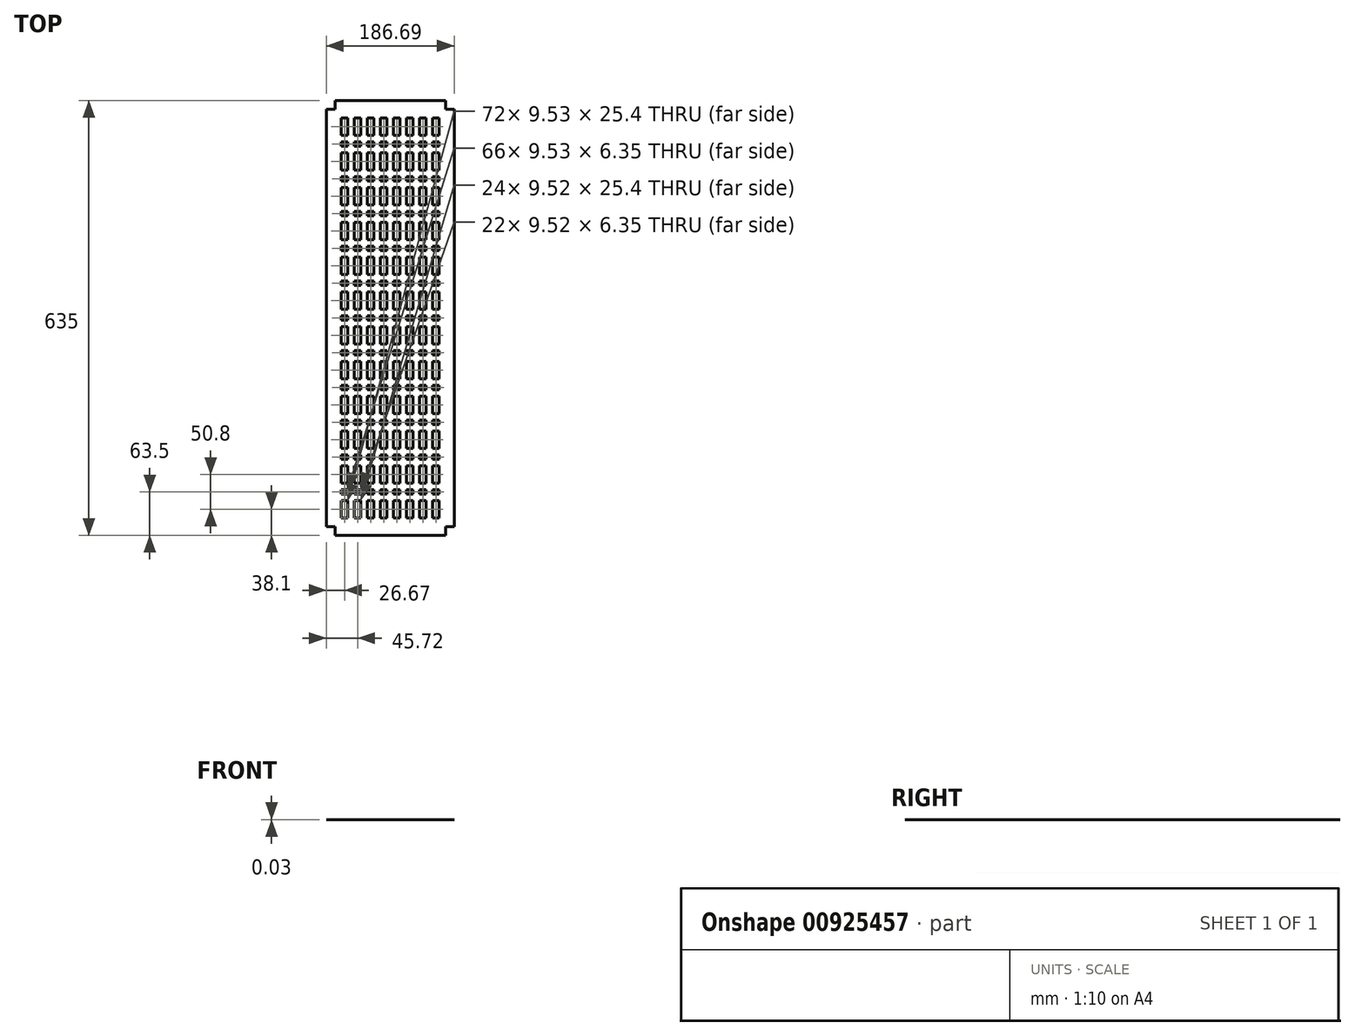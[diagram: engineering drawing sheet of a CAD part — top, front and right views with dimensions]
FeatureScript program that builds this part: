
annotation { "Feature Type Name" : "Feature", "Feature Type Description" : "" }
export const myFeature = defineFeature(function(context is Context, id is Id, definition is map)
    precondition{}
    {
        {
            var Q0;
            Q0=qCreatedBy(makeId("Top.planeOp"),FACE);
            var sketch = newSketch(context, id + "F0", { "sketchPlane" : qUnion([Q0])});
            skLineSegment(sketch, "E0", {"start": v(0, 0) * mm, "end": v(0, 12.7) * mm});
            skLineSegment(sketch, "E1", {"start": v(0, 12.7) * mm, "end": v(161.3, 12.7) * mm});
            skLineSegment(sketch, "E2", {"start": v(161.3, 12.7) * mm, "end": v(161.3, 0) * mm});
            skLineSegment(sketch, "E3", {"start": v(161.3, 0) * mm, "end": v(174, 0) * mm});
            skLineSegment(sketch, "E4", {"start": v(174, 0) * mm, "end": v(174, -609.6) * mm});
            skLineSegment(sketch, "E5", {"start": v(174, -609.6) * mm, "end": v(161.3, -609.6) * mm});
            skLineSegment(sketch, "E6", {"start": v(161.3, -609.6) * mm, "end": v(161.3, -622.3) * mm});
            skLineSegment(sketch, "E7", {"start": v(161.3, -622.3) * mm, "end": v(0, -622.3) * mm});
            skLineSegment(sketch, "E8", {"start": v(0, -622.3) * mm, "end": v(0, -609.6) * mm});
            skLineSegment(sketch, "E9", {"start": v(0, -609.6) * mm, "end": v(-12.7, -609.6) * mm});
            skLineSegment(sketch, "E10", {"start": v(-12.7, -609.6) * mm, "end": v(-12.7, 0) * mm});
            skLineSegment(sketch, "E11", {"start": v(-12.7, 0) * mm, "end": v(0, 0) * mm});
            skSolve(sketch);
        }
        {
            var Q0;
            Q0 = qSketchRegion(id + "F0", true);
            extrude(context, id + "F1", {"entities" : qUnion([Q0]), "depth" : 0.03 * mm, "offsetDistance" : 25.4 * mm});
        }
        {
            var Q0;
            Q0=makeQuery(id+"F1.opExtrude","CAP_FACE",FACE,{"disambiguationData":[OSD([sQuery(id+"F0.wireOp",EDGE,"E0"),sQuery(id+"F0.wireOp",EDGE,"E1"),sQuery(id+"F0.wireOp",EDGE,"E2"),sQuery(id+"F0.wireOp",EDGE,"E3"),sQuery(id+"F0.wireOp",EDGE,"E4"),sQuery(id+"F0.wireOp",EDGE,"E5"),sQuery(id+"F0.wireOp",EDGE,"E6"),sQuery(id+"F0.wireOp",EDGE,"E7"),sQuery(id+"F0.wireOp",EDGE,"E8"),sQuery(id+"F0.wireOp",EDGE,"E9"),sQuery(id+"F0.wireOp",EDGE,"E10"),sQuery(id+"F0.wireOp",EDGE,"E11")])],"isStart":false});
            var sketch = newSketch(context, id + "F2", { "sketchPlane" : qUnion([Q0])});
            skLineSegment(sketch, "E12", {"start": v(80.65, 12.7) * mm, "end": v(80.65, -622.3) * mm, "construction": true});
            skLineSegment(sketch, "E13.bottom", {"start": v(75.88, -12.7) * mm, "end": v(66.36, -12.7) * mm});
            skLineSegment(sketch, "E13.top", {"start": v(75.88, -38.1) * mm, "end": v(66.36, -38.1) * mm});
            skLineSegment(sketch, "E13.left", {"start": v(75.88, -12.7) * mm, "end": v(75.88, -38.1) * mm});
            skLineSegment(sketch, "E13.right", {"start": v(66.36, -12.7) * mm, "end": v(66.36, -38.1) * mm});
            skLineSegment(sketch, "E14.bottom", {"start": v(66.36, -47.63) * mm, "end": v(75.88, -47.63) * mm});
            skLineSegment(sketch, "E14.top", {"start": v(66.36, -53.98) * mm, "end": v(75.88, -53.98) * mm});
            skLineSegment(sketch, "E14.left", {"start": v(66.36, -47.63) * mm, "end": v(66.36, -53.98) * mm});
            skLineSegment(sketch, "E14.right", {"start": v(75.88, -47.63) * mm, "end": v(75.88, -53.98) * mm});
            skLineSegment(sketch, "E15.0.1.0", {"start": v(66.36, -63.5) * mm, "end": v(66.36, -88.9) * mm});
            skLineSegment(sketch, "E15.0.1.1", {"start": v(75.88, -63.5) * mm, "end": v(66.36, -63.5) * mm});
            skLineSegment(sketch, "E15.0.1.2", {"start": v(75.88, -63.5) * mm, "end": v(75.88, -88.9) * mm});
            skLineSegment(sketch, "E15.0.1.3", {"start": v(75.88, -88.9) * mm, "end": v(66.36, -88.9) * mm});
            skLineSegment(sketch, "E15.0.1.4", {"start": v(66.36, -98.43) * mm, "end": v(75.88, -98.43) * mm});
            skLineSegment(sketch, "E15.0.1.5", {"start": v(75.88, -98.43) * mm, "end": v(75.88, -104.78) * mm});
            skLineSegment(sketch, "E15.0.1.6", {"start": v(66.36, -104.78) * mm, "end": v(75.88, -104.78) * mm});
            skLineSegment(sketch, "E15.0.1.7", {"start": v(66.36, -98.43) * mm, "end": v(66.36, -104.78) * mm});
            skLineSegment(sketch, "E15.0.2.0", {"start": v(66.36, -114.3) * mm, "end": v(66.36, -139.7) * mm});
            skLineSegment(sketch, "E15.0.2.1", {"start": v(75.88, -114.3) * mm, "end": v(66.36, -114.3) * mm});
            skLineSegment(sketch, "E15.0.2.2", {"start": v(75.88, -114.3) * mm, "end": v(75.88, -139.7) * mm});
            skLineSegment(sketch, "E15.0.2.3", {"start": v(75.88, -139.7) * mm, "end": v(66.36, -139.7) * mm});
            skLineSegment(sketch, "E15.0.2.4", {"start": v(66.36, -149.22) * mm, "end": v(75.88, -149.22) * mm});
            skLineSegment(sketch, "E15.0.2.5", {"start": v(75.88, -149.23) * mm, "end": v(75.88, -155.58) * mm});
            skLineSegment(sketch, "E15.0.2.6", {"start": v(66.36, -155.58) * mm, "end": v(75.88, -155.58) * mm});
            skLineSegment(sketch, "E15.0.2.7", {"start": v(66.36, -149.23) * mm, "end": v(66.36, -155.58) * mm});
            skLineSegment(sketch, "E15.0.3.0", {"start": v(66.36, -165.1) * mm, "end": v(66.36, -190.5) * mm});
            skLineSegment(sketch, "E15.0.3.1", {"start": v(75.88, -165.1) * mm, "end": v(66.36, -165.1) * mm});
            skLineSegment(sketch, "E15.0.3.2", {"start": v(75.88, -165.1) * mm, "end": v(75.88, -190.5) * mm});
            skLineSegment(sketch, "E15.0.3.3", {"start": v(75.88, -190.5) * mm, "end": v(66.36, -190.5) * mm});
            skLineSegment(sketch, "E15.0.3.4", {"start": v(66.36, -200.02) * mm, "end": v(75.88, -200.02) * mm});
            skLineSegment(sketch, "E15.0.3.5", {"start": v(75.88, -200.02) * mm, "end": v(75.88, -206.37) * mm});
            skLineSegment(sketch, "E15.0.3.6", {"start": v(66.36, -206.37) * mm, "end": v(75.88, -206.37) * mm});
            skLineSegment(sketch, "E15.0.3.7", {"start": v(66.36, -200.02) * mm, "end": v(66.36, -206.37) * mm});
            skLineSegment(sketch, "E15.0.4.0", {"start": v(66.36, -215.9) * mm, "end": v(66.36, -241.3) * mm});
            skLineSegment(sketch, "E15.0.4.1", {"start": v(75.88, -215.9) * mm, "end": v(66.36, -215.9) * mm});
            skLineSegment(sketch, "E15.0.4.2", {"start": v(75.88, -215.9) * mm, "end": v(75.88, -241.3) * mm});
            skLineSegment(sketch, "E15.0.4.3", {"start": v(75.88, -241.3) * mm, "end": v(66.36, -241.3) * mm});
            skLineSegment(sketch, "E15.0.4.4", {"start": v(66.36, -250.83) * mm, "end": v(75.88, -250.83) * mm});
            skLineSegment(sketch, "E15.0.4.5", {"start": v(75.88, -250.82) * mm, "end": v(75.88, -257.18) * mm});
            skLineSegment(sketch, "E15.0.4.6", {"start": v(66.36, -257.18) * mm, "end": v(75.88, -257.18) * mm});
            skLineSegment(sketch, "E15.0.4.7", {"start": v(66.36, -250.82) * mm, "end": v(66.36, -257.18) * mm});
            skLineSegment(sketch, "E15.0.5.0", {"start": v(66.36, -266.7) * mm, "end": v(66.36, -292.1) * mm});
            skLineSegment(sketch, "E15.0.5.1", {"start": v(75.88, -266.7) * mm, "end": v(66.36, -266.7) * mm});
            skLineSegment(sketch, "E15.0.5.2", {"start": v(75.88, -266.7) * mm, "end": v(75.88, -292.1) * mm});
            skLineSegment(sketch, "E15.0.5.3", {"start": v(75.88, -292.1) * mm, "end": v(66.36, -292.1) * mm});
            skLineSegment(sketch, "E15.0.5.4", {"start": v(66.36, -301.63) * mm, "end": v(75.88, -301.63) * mm});
            skLineSegment(sketch, "E15.0.5.5", {"start": v(75.88, -301.62) * mm, "end": v(75.88, -307.98) * mm});
            skLineSegment(sketch, "E15.0.5.6", {"start": v(66.36, -307.98) * mm, "end": v(75.88, -307.98) * mm});
            skLineSegment(sketch, "E15.0.5.7", {"start": v(66.36, -301.62) * mm, "end": v(66.36, -307.98) * mm});
            skLineSegment(sketch, "E15.0.6.0", {"start": v(66.36, -317.5) * mm, "end": v(66.36, -342.9) * mm});
            skLineSegment(sketch, "E15.0.6.1", {"start": v(75.88, -317.5) * mm, "end": v(66.36, -317.5) * mm});
            skLineSegment(sketch, "E15.0.6.2", {"start": v(75.88, -317.5) * mm, "end": v(75.88, -342.9) * mm});
            skLineSegment(sketch, "E15.0.6.3", {"start": v(75.88, -342.9) * mm, "end": v(66.36, -342.9) * mm});
            skLineSegment(sketch, "E15.0.6.4", {"start": v(66.36, -352.43) * mm, "end": v(75.88, -352.43) * mm});
            skLineSegment(sketch, "E15.0.6.5", {"start": v(75.88, -352.42) * mm, "end": v(75.88, -358.77) * mm});
            skLineSegment(sketch, "E15.0.6.6", {"start": v(66.36, -358.77) * mm, "end": v(75.88, -358.77) * mm});
            skLineSegment(sketch, "E15.0.6.7", {"start": v(66.36, -352.42) * mm, "end": v(66.36, -358.77) * mm});
            skLineSegment(sketch, "E15.0.7.0", {"start": v(66.36, -368.3) * mm, "end": v(66.36, -393.7) * mm});
            skLineSegment(sketch, "E15.0.7.1", {"start": v(75.88, -368.3) * mm, "end": v(66.36, -368.3) * mm});
            skLineSegment(sketch, "E15.0.7.2", {"start": v(75.88, -368.3) * mm, "end": v(75.88, -393.7) * mm});
            skLineSegment(sketch, "E15.0.7.3", {"start": v(75.88, -393.7) * mm, "end": v(66.36, -393.7) * mm});
            skLineSegment(sketch, "E15.0.7.4", {"start": v(66.36, -403.23) * mm, "end": v(75.88, -403.23) * mm});
            skLineSegment(sketch, "E15.0.7.5", {"start": v(75.88, -403.22) * mm, "end": v(75.88, -409.57) * mm});
            skLineSegment(sketch, "E15.0.7.6", {"start": v(66.36, -409.57) * mm, "end": v(75.88, -409.57) * mm});
            skLineSegment(sketch, "E15.0.7.7", {"start": v(66.36, -403.22) * mm, "end": v(66.36, -409.57) * mm});
            skLineSegment(sketch, "E15.0.8.0", {"start": v(66.36, -419.1) * mm, "end": v(66.36, -444.5) * mm});
            skLineSegment(sketch, "E15.0.8.1", {"start": v(75.88, -419.1) * mm, "end": v(66.36, -419.1) * mm});
            skLineSegment(sketch, "E15.0.8.2", {"start": v(75.88, -419.1) * mm, "end": v(75.88, -444.5) * mm});
            skLineSegment(sketch, "E15.0.8.3", {"start": v(75.88, -444.5) * mm, "end": v(66.36, -444.5) * mm});
            skLineSegment(sketch, "E15.0.8.4", {"start": v(66.36, -454.03) * mm, "end": v(75.88, -454.03) * mm});
            skLineSegment(sketch, "E15.0.8.5", {"start": v(75.88, -454.02) * mm, "end": v(75.88, -460.38) * mm});
            skLineSegment(sketch, "E15.0.8.6", {"start": v(66.36, -460.38) * mm, "end": v(75.88, -460.38) * mm});
            skLineSegment(sketch, "E15.0.8.7", {"start": v(66.36, -454.02) * mm, "end": v(66.36, -460.38) * mm});
            skLineSegment(sketch, "E15.0.9.0", {"start": v(66.36, -469.9) * mm, "end": v(66.36, -495.3) * mm});
            skLineSegment(sketch, "E15.0.9.1", {"start": v(75.88, -469.9) * mm, "end": v(66.36, -469.9) * mm});
            skLineSegment(sketch, "E15.0.9.2", {"start": v(75.88, -469.9) * mm, "end": v(75.88, -495.3) * mm});
            skLineSegment(sketch, "E15.0.9.3", {"start": v(75.88, -495.3) * mm, "end": v(66.36, -495.3) * mm});
            skLineSegment(sketch, "E15.0.9.4", {"start": v(66.36, -504.82) * mm, "end": v(75.88, -504.82) * mm});
            skLineSegment(sketch, "E15.0.9.5", {"start": v(75.88, -504.82) * mm, "end": v(75.88, -511.17) * mm});
            skLineSegment(sketch, "E15.0.9.6", {"start": v(66.36, -511.18) * mm, "end": v(75.88, -511.18) * mm});
            skLineSegment(sketch, "E15.0.9.7", {"start": v(66.36, -504.82) * mm, "end": v(66.36, -511.17) * mm});
            skLineSegment(sketch, "E15.0.10.0", {"start": v(66.36, -520.7) * mm, "end": v(66.36, -546.1) * mm});
            skLineSegment(sketch, "E15.0.10.1", {"start": v(75.88, -520.7) * mm, "end": v(66.36, -520.7) * mm});
            skLineSegment(sketch, "E15.0.10.2", {"start": v(75.88, -520.7) * mm, "end": v(75.88, -546.1) * mm});
            skLineSegment(sketch, "E15.0.10.3", {"start": v(75.88, -546.1) * mm, "end": v(66.36, -546.1) * mm});
            skLineSegment(sketch, "E15.0.10.4", {"start": v(66.36, -555.62) * mm, "end": v(75.88, -555.62) * mm});
            skLineSegment(sketch, "E15.0.10.5", {"start": v(75.88, -555.62) * mm, "end": v(75.88, -561.98) * mm});
            skLineSegment(sketch, "E15.0.10.6", {"start": v(66.36, -561.98) * mm, "end": v(75.88, -561.98) * mm});
            skLineSegment(sketch, "E15.0.10.7", {"start": v(66.36, -555.62) * mm, "end": v(66.36, -561.98) * mm});
            skLineSegment(sketch, "E15.0.11.0", {"start": v(66.36, -571.5) * mm, "end": v(66.36, -596.9) * mm});
            skLineSegment(sketch, "E15.0.11.1", {"start": v(75.88, -571.5) * mm, "end": v(66.36, -571.5) * mm});
            skLineSegment(sketch, "E15.0.11.2", {"start": v(75.88, -571.5) * mm, "end": v(75.88, -596.9) * mm});
            skLineSegment(sketch, "E15.0.11.3", {"start": v(75.88, -596.9) * mm, "end": v(66.36, -596.9) * mm});
            skLineSegment(sketch, "E15.1.0.0", {"start": v(47.3, -12.7) * mm, "end": v(47.3, -38.1) * mm});
            skLineSegment(sketch, "E15.1.0.1", {"start": v(56.83, -12.7) * mm, "end": v(47.3, -12.7) * mm});
            skLineSegment(sketch, "E15.1.0.2", {"start": v(56.83, -12.7) * mm, "end": v(56.83, -38.1) * mm});
            skLineSegment(sketch, "E15.1.0.3", {"start": v(56.83, -38.1) * mm, "end": v(47.3, -38.1) * mm});
            skLineSegment(sketch, "E15.1.0.4", {"start": v(47.3, -47.63) * mm, "end": v(56.83, -47.63) * mm});
            skLineSegment(sketch, "E15.1.0.5", {"start": v(56.83, -47.63) * mm, "end": v(56.83, -53.98) * mm});
            skLineSegment(sketch, "E15.1.0.6", {"start": v(47.3, -53.98) * mm, "end": v(56.83, -53.98) * mm});
            skLineSegment(sketch, "E15.1.0.7", {"start": v(47.3, -47.63) * mm, "end": v(47.3, -53.98) * mm});
            skLineSegment(sketch, "E15.1.1.0", {"start": v(47.3, -63.5) * mm, "end": v(47.3, -88.9) * mm});
            skLineSegment(sketch, "E15.1.1.1", {"start": v(56.83, -63.5) * mm, "end": v(47.3, -63.5) * mm});
            skLineSegment(sketch, "E15.1.1.2", {"start": v(56.83, -63.5) * mm, "end": v(56.83, -88.9) * mm});
            skLineSegment(sketch, "E15.1.1.3", {"start": v(56.83, -88.9) * mm, "end": v(47.3, -88.9) * mm});
            skLineSegment(sketch, "E15.1.1.4", {"start": v(47.3, -98.43) * mm, "end": v(56.83, -98.43) * mm});
            skLineSegment(sketch, "E15.1.1.5", {"start": v(56.83, -98.43) * mm, "end": v(56.83, -104.78) * mm});
            skLineSegment(sketch, "E15.1.1.6", {"start": v(47.3, -104.78) * mm, "end": v(56.83, -104.78) * mm});
            skLineSegment(sketch, "E15.1.1.7", {"start": v(47.3, -98.43) * mm, "end": v(47.3, -104.78) * mm});
            skLineSegment(sketch, "E15.1.2.0", {"start": v(47.3, -114.3) * mm, "end": v(47.3, -139.7) * mm});
            skLineSegment(sketch, "E15.1.2.1", {"start": v(56.83, -114.3) * mm, "end": v(47.3, -114.3) * mm});
            skLineSegment(sketch, "E15.1.2.2", {"start": v(56.83, -114.3) * mm, "end": v(56.83, -139.7) * mm});
            skLineSegment(sketch, "E15.1.2.3", {"start": v(56.83, -139.7) * mm, "end": v(47.3, -139.7) * mm});
            skLineSegment(sketch, "E15.1.2.4", {"start": v(47.3, -149.22) * mm, "end": v(56.83, -149.22) * mm});
            skLineSegment(sketch, "E15.1.2.5", {"start": v(56.83, -149.23) * mm, "end": v(56.83, -155.58) * mm});
            skLineSegment(sketch, "E15.1.2.6", {"start": v(47.3, -155.58) * mm, "end": v(56.83, -155.58) * mm});
            skLineSegment(sketch, "E15.1.2.7", {"start": v(47.3, -149.23) * mm, "end": v(47.3, -155.58) * mm});
            skLineSegment(sketch, "E15.1.3.0", {"start": v(47.3, -165.1) * mm, "end": v(47.3, -190.5) * mm});
            skLineSegment(sketch, "E15.1.3.1", {"start": v(56.83, -165.1) * mm, "end": v(47.3, -165.1) * mm});
            skLineSegment(sketch, "E15.1.3.2", {"start": v(56.83, -165.1) * mm, "end": v(56.83, -190.5) * mm});
            skLineSegment(sketch, "E15.1.3.3", {"start": v(56.83, -190.5) * mm, "end": v(47.3, -190.5) * mm});
            skLineSegment(sketch, "E15.1.3.4", {"start": v(47.3, -200.02) * mm, "end": v(56.83, -200.02) * mm});
            skLineSegment(sketch, "E15.1.3.5", {"start": v(56.83, -200.02) * mm, "end": v(56.83, -206.37) * mm});
            skLineSegment(sketch, "E15.1.3.6", {"start": v(47.3, -206.37) * mm, "end": v(56.83, -206.37) * mm});
            skLineSegment(sketch, "E15.1.3.7", {"start": v(47.3, -200.02) * mm, "end": v(47.3, -206.37) * mm});
            skLineSegment(sketch, "E15.1.4.0", {"start": v(47.3, -215.9) * mm, "end": v(47.3, -241.3) * mm});
            skLineSegment(sketch, "E15.1.4.1", {"start": v(56.83, -215.9) * mm, "end": v(47.3, -215.9) * mm});
            skLineSegment(sketch, "E15.1.4.2", {"start": v(56.83, -215.9) * mm, "end": v(56.83, -241.3) * mm});
            skLineSegment(sketch, "E15.1.4.3", {"start": v(56.83, -241.3) * mm, "end": v(47.3, -241.3) * mm});
            skLineSegment(sketch, "E15.1.4.4", {"start": v(47.3, -250.83) * mm, "end": v(56.83, -250.83) * mm});
            skLineSegment(sketch, "E15.1.4.5", {"start": v(56.83, -250.82) * mm, "end": v(56.83, -257.18) * mm});
            skLineSegment(sketch, "E15.1.4.6", {"start": v(47.3, -257.18) * mm, "end": v(56.83, -257.18) * mm});
            skLineSegment(sketch, "E15.1.4.7", {"start": v(47.3, -250.82) * mm, "end": v(47.3, -257.18) * mm});
            skLineSegment(sketch, "E15.1.5.0", {"start": v(47.3, -266.7) * mm, "end": v(47.3, -292.1) * mm});
            skLineSegment(sketch, "E15.1.5.1", {"start": v(56.83, -266.7) * mm, "end": v(47.3, -266.7) * mm});
            skLineSegment(sketch, "E15.1.5.2", {"start": v(56.83, -266.7) * mm, "end": v(56.83, -292.1) * mm});
            skLineSegment(sketch, "E15.1.5.3", {"start": v(56.83, -292.1) * mm, "end": v(47.3, -292.1) * mm});
            skLineSegment(sketch, "E15.1.5.4", {"start": v(47.3, -301.63) * mm, "end": v(56.83, -301.63) * mm});
            skLineSegment(sketch, "E15.1.5.5", {"start": v(56.83, -301.62) * mm, "end": v(56.83, -307.98) * mm});
            skLineSegment(sketch, "E15.1.5.6", {"start": v(47.3, -307.98) * mm, "end": v(56.83, -307.98) * mm});
            skLineSegment(sketch, "E15.1.5.7", {"start": v(47.3, -301.62) * mm, "end": v(47.3, -307.98) * mm});
            skLineSegment(sketch, "E15.1.6.0", {"start": v(47.3, -317.5) * mm, "end": v(47.3, -342.9) * mm});
            skLineSegment(sketch, "E15.1.6.1", {"start": v(56.83, -317.5) * mm, "end": v(47.3, -317.5) * mm});
            skLineSegment(sketch, "E15.1.6.2", {"start": v(56.83, -317.5) * mm, "end": v(56.83, -342.9) * mm});
            skLineSegment(sketch, "E15.1.6.3", {"start": v(56.83, -342.9) * mm, "end": v(47.3, -342.9) * mm});
            skLineSegment(sketch, "E15.1.6.4", {"start": v(47.3, -352.43) * mm, "end": v(56.83, -352.43) * mm});
            skLineSegment(sketch, "E15.1.6.5", {"start": v(56.83, -352.42) * mm, "end": v(56.83, -358.77) * mm});
            skLineSegment(sketch, "E15.1.6.6", {"start": v(47.3, -358.77) * mm, "end": v(56.83, -358.77) * mm});
            skLineSegment(sketch, "E15.1.6.7", {"start": v(47.3, -352.42) * mm, "end": v(47.3, -358.77) * mm});
            skLineSegment(sketch, "E15.1.7.0", {"start": v(47.3, -368.3) * mm, "end": v(47.3, -393.7) * mm});
            skLineSegment(sketch, "E15.1.7.1", {"start": v(56.83, -368.3) * mm, "end": v(47.3, -368.3) * mm});
            skLineSegment(sketch, "E15.1.7.2", {"start": v(56.83, -368.3) * mm, "end": v(56.83, -393.7) * mm});
            skLineSegment(sketch, "E15.1.7.3", {"start": v(56.83, -393.7) * mm, "end": v(47.3, -393.7) * mm});
            skLineSegment(sketch, "E15.1.7.4", {"start": v(47.3, -403.23) * mm, "end": v(56.83, -403.23) * mm});
            skLineSegment(sketch, "E15.1.7.5", {"start": v(56.83, -403.22) * mm, "end": v(56.83, -409.57) * mm});
            skLineSegment(sketch, "E15.1.7.6", {"start": v(47.3, -409.57) * mm, "end": v(56.83, -409.57) * mm});
            skLineSegment(sketch, "E15.1.7.7", {"start": v(47.3, -403.22) * mm, "end": v(47.3, -409.57) * mm});
            skLineSegment(sketch, "E15.1.8.0", {"start": v(47.3, -419.1) * mm, "end": v(47.3, -444.5) * mm});
            skLineSegment(sketch, "E15.1.8.1", {"start": v(56.83, -419.1) * mm, "end": v(47.3, -419.1) * mm});
            skLineSegment(sketch, "E15.1.8.2", {"start": v(56.83, -419.1) * mm, "end": v(56.83, -444.5) * mm});
            skLineSegment(sketch, "E15.1.8.3", {"start": v(56.83, -444.5) * mm, "end": v(47.3, -444.5) * mm});
            skLineSegment(sketch, "E15.1.8.4", {"start": v(47.3, -454.03) * mm, "end": v(56.83, -454.03) * mm});
            skLineSegment(sketch, "E15.1.8.5", {"start": v(56.83, -454.02) * mm, "end": v(56.83, -460.38) * mm});
            skLineSegment(sketch, "E15.1.8.6", {"start": v(47.3, -460.38) * mm, "end": v(56.83, -460.38) * mm});
            skLineSegment(sketch, "E15.1.8.7", {"start": v(47.3, -454.02) * mm, "end": v(47.3, -460.38) * mm});
            skLineSegment(sketch, "E15.1.9.0", {"start": v(47.3, -469.9) * mm, "end": v(47.3, -495.3) * mm});
            skLineSegment(sketch, "E15.1.9.1", {"start": v(56.83, -469.9) * mm, "end": v(47.3, -469.9) * mm});
            skLineSegment(sketch, "E15.1.9.2", {"start": v(56.83, -469.9) * mm, "end": v(56.83, -495.3) * mm});
            skLineSegment(sketch, "E15.1.9.3", {"start": v(56.83, -495.3) * mm, "end": v(47.3, -495.3) * mm});
            skLineSegment(sketch, "E15.1.9.4", {"start": v(47.3, -504.82) * mm, "end": v(56.83, -504.82) * mm});
            skLineSegment(sketch, "E15.1.9.5", {"start": v(56.83, -504.82) * mm, "end": v(56.83, -511.17) * mm});
            skLineSegment(sketch, "E15.1.9.6", {"start": v(47.3, -511.18) * mm, "end": v(56.83, -511.18) * mm});
            skLineSegment(sketch, "E15.1.9.7", {"start": v(47.3, -504.82) * mm, "end": v(47.3, -511.17) * mm});
            skLineSegment(sketch, "E15.1.10.0", {"start": v(47.3, -520.7) * mm, "end": v(47.3, -546.1) * mm});
            skLineSegment(sketch, "E15.1.10.1", {"start": v(56.83, -520.7) * mm, "end": v(47.3, -520.7) * mm});
            skLineSegment(sketch, "E15.1.10.2", {"start": v(56.83, -520.7) * mm, "end": v(56.83, -546.1) * mm});
            skLineSegment(sketch, "E15.1.10.3", {"start": v(56.83, -546.1) * mm, "end": v(47.3, -546.1) * mm});
            skLineSegment(sketch, "E15.1.10.4", {"start": v(47.3, -555.62) * mm, "end": v(56.83, -555.62) * mm});
            skLineSegment(sketch, "E15.1.10.5", {"start": v(56.83, -555.62) * mm, "end": v(56.83, -561.98) * mm});
            skLineSegment(sketch, "E15.1.10.6", {"start": v(47.3, -561.98) * mm, "end": v(56.83, -561.98) * mm});
            skLineSegment(sketch, "E15.1.10.7", {"start": v(47.3, -555.62) * mm, "end": v(47.3, -561.98) * mm});
            skLineSegment(sketch, "E15.1.11.0", {"start": v(47.3, -571.5) * mm, "end": v(47.3, -596.9) * mm});
            skLineSegment(sketch, "E15.1.11.1", {"start": v(56.83, -571.5) * mm, "end": v(47.3, -571.5) * mm});
            skLineSegment(sketch, "E15.1.11.2", {"start": v(56.83, -571.5) * mm, "end": v(56.83, -596.9) * mm});
            skLineSegment(sketch, "E15.1.11.3", {"start": v(56.83, -596.9) * mm, "end": v(47.3, -596.9) * mm});
            skLineSegment(sketch, "E15.2.0.0", {"start": v(28.26, -12.7) * mm, "end": v(28.26, -38.1) * mm});
            skLineSegment(sketch, "E15.2.0.1", {"start": v(37.78, -12.7) * mm, "end": v(28.26, -12.7) * mm});
            skLineSegment(sketch, "E15.2.0.2", {"start": v(37.78, -12.7) * mm, "end": v(37.78, -38.1) * mm});
            skLineSegment(sketch, "E15.2.0.3", {"start": v(37.78, -38.1) * mm, "end": v(28.26, -38.1) * mm});
            skLineSegment(sketch, "E15.2.0.4", {"start": v(28.26, -47.63) * mm, "end": v(37.78, -47.63) * mm});
            skLineSegment(sketch, "E15.2.0.5", {"start": v(37.78, -47.63) * mm, "end": v(37.78, -53.98) * mm});
            skLineSegment(sketch, "E15.2.0.6", {"start": v(28.26, -53.98) * mm, "end": v(37.78, -53.98) * mm});
            skLineSegment(sketch, "E15.2.0.7", {"start": v(28.26, -47.63) * mm, "end": v(28.26, -53.98) * mm});
            skLineSegment(sketch, "E15.2.1.0", {"start": v(28.26, -63.5) * mm, "end": v(28.26, -88.9) * mm});
            skLineSegment(sketch, "E15.2.1.1", {"start": v(37.78, -63.5) * mm, "end": v(28.26, -63.5) * mm});
            skLineSegment(sketch, "E15.2.1.2", {"start": v(37.78, -63.5) * mm, "end": v(37.78, -88.9) * mm});
            skLineSegment(sketch, "E15.2.1.3", {"start": v(37.78, -88.9) * mm, "end": v(28.26, -88.9) * mm});
            skLineSegment(sketch, "E15.2.1.4", {"start": v(28.26, -98.43) * mm, "end": v(37.78, -98.43) * mm});
            skLineSegment(sketch, "E15.2.1.5", {"start": v(37.78, -98.43) * mm, "end": v(37.78, -104.78) * mm});
            skLineSegment(sketch, "E15.2.1.6", {"start": v(28.26, -104.78) * mm, "end": v(37.78, -104.78) * mm});
            skLineSegment(sketch, "E15.2.1.7", {"start": v(28.26, -98.43) * mm, "end": v(28.26, -104.78) * mm});
            skLineSegment(sketch, "E15.2.2.0", {"start": v(28.26, -114.3) * mm, "end": v(28.26, -139.7) * mm});
            skLineSegment(sketch, "E15.2.2.1", {"start": v(37.78, -114.3) * mm, "end": v(28.26, -114.3) * mm});
            skLineSegment(sketch, "E15.2.2.2", {"start": v(37.78, -114.3) * mm, "end": v(37.78, -139.7) * mm});
            skLineSegment(sketch, "E15.2.2.3", {"start": v(37.78, -139.7) * mm, "end": v(28.26, -139.7) * mm});
            skLineSegment(sketch, "E15.2.2.4", {"start": v(28.26, -149.22) * mm, "end": v(37.78, -149.22) * mm});
            skLineSegment(sketch, "E15.2.2.5", {"start": v(37.78, -149.23) * mm, "end": v(37.78, -155.58) * mm});
            skLineSegment(sketch, "E15.2.2.6", {"start": v(28.26, -155.58) * mm, "end": v(37.78, -155.58) * mm});
            skLineSegment(sketch, "E15.2.2.7", {"start": v(28.26, -149.23) * mm, "end": v(28.26, -155.58) * mm});
            skLineSegment(sketch, "E15.2.3.0", {"start": v(28.26, -165.1) * mm, "end": v(28.26, -190.5) * mm});
            skLineSegment(sketch, "E15.2.3.1", {"start": v(37.78, -165.1) * mm, "end": v(28.26, -165.1) * mm});
            skLineSegment(sketch, "E15.2.3.2", {"start": v(37.78, -165.1) * mm, "end": v(37.78, -190.5) * mm});
            skLineSegment(sketch, "E15.2.3.3", {"start": v(37.78, -190.5) * mm, "end": v(28.26, -190.5) * mm});
            skLineSegment(sketch, "E15.2.3.4", {"start": v(28.26, -200.02) * mm, "end": v(37.78, -200.02) * mm});
            skLineSegment(sketch, "E15.2.3.5", {"start": v(37.78, -200.02) * mm, "end": v(37.78, -206.37) * mm});
            skLineSegment(sketch, "E15.2.3.6", {"start": v(28.26, -206.37) * mm, "end": v(37.78, -206.37) * mm});
            skLineSegment(sketch, "E15.2.3.7", {"start": v(28.26, -200.02) * mm, "end": v(28.26, -206.37) * mm});
            skLineSegment(sketch, "E15.2.4.0", {"start": v(28.26, -215.9) * mm, "end": v(28.26, -241.3) * mm});
            skLineSegment(sketch, "E15.2.4.1", {"start": v(37.78, -215.9) * mm, "end": v(28.26, -215.9) * mm});
            skLineSegment(sketch, "E15.2.4.2", {"start": v(37.78, -215.9) * mm, "end": v(37.78, -241.3) * mm});
            skLineSegment(sketch, "E15.2.4.3", {"start": v(37.78, -241.3) * mm, "end": v(28.26, -241.3) * mm});
            skLineSegment(sketch, "E15.2.4.4", {"start": v(28.26, -250.83) * mm, "end": v(37.78, -250.83) * mm});
            skLineSegment(sketch, "E15.2.4.5", {"start": v(37.78, -250.82) * mm, "end": v(37.78, -257.18) * mm});
            skLineSegment(sketch, "E15.2.4.6", {"start": v(28.26, -257.18) * mm, "end": v(37.78, -257.18) * mm});
            skLineSegment(sketch, "E15.2.4.7", {"start": v(28.26, -250.82) * mm, "end": v(28.26, -257.18) * mm});
            skLineSegment(sketch, "E15.2.5.0", {"start": v(28.26, -266.7) * mm, "end": v(28.26, -292.1) * mm});
            skLineSegment(sketch, "E15.2.5.1", {"start": v(37.78, -266.7) * mm, "end": v(28.26, -266.7) * mm});
            skLineSegment(sketch, "E15.2.5.2", {"start": v(37.78, -266.7) * mm, "end": v(37.78, -292.1) * mm});
            skLineSegment(sketch, "E15.2.5.3", {"start": v(37.78, -292.1) * mm, "end": v(28.26, -292.1) * mm});
            skLineSegment(sketch, "E15.2.5.4", {"start": v(28.26, -301.63) * mm, "end": v(37.78, -301.63) * mm});
            skLineSegment(sketch, "E15.2.5.5", {"start": v(37.78, -301.62) * mm, "end": v(37.78, -307.98) * mm});
            skLineSegment(sketch, "E15.2.5.6", {"start": v(28.26, -307.98) * mm, "end": v(37.78, -307.98) * mm});
            skLineSegment(sketch, "E15.2.5.7", {"start": v(28.26, -301.62) * mm, "end": v(28.26, -307.98) * mm});
            skLineSegment(sketch, "E15.2.6.0", {"start": v(28.26, -317.5) * mm, "end": v(28.26, -342.9) * mm});
            skLineSegment(sketch, "E15.2.6.1", {"start": v(37.78, -317.5) * mm, "end": v(28.26, -317.5) * mm});
            skLineSegment(sketch, "E15.2.6.2", {"start": v(37.78, -317.5) * mm, "end": v(37.78, -342.9) * mm});
            skLineSegment(sketch, "E15.2.6.3", {"start": v(37.78, -342.9) * mm, "end": v(28.26, -342.9) * mm});
            skLineSegment(sketch, "E15.2.6.4", {"start": v(28.26, -352.43) * mm, "end": v(37.78, -352.43) * mm});
            skLineSegment(sketch, "E15.2.6.5", {"start": v(37.78, -352.42) * mm, "end": v(37.78, -358.77) * mm});
            skLineSegment(sketch, "E15.2.6.6", {"start": v(28.26, -358.77) * mm, "end": v(37.78, -358.77) * mm});
            skLineSegment(sketch, "E15.2.6.7", {"start": v(28.26, -352.42) * mm, "end": v(28.26, -358.77) * mm});
            skLineSegment(sketch, "E15.2.7.0", {"start": v(28.26, -368.3) * mm, "end": v(28.26, -393.7) * mm});
            skLineSegment(sketch, "E15.2.7.1", {"start": v(37.78, -368.3) * mm, "end": v(28.26, -368.3) * mm});
            skLineSegment(sketch, "E15.2.7.2", {"start": v(37.78, -368.3) * mm, "end": v(37.78, -393.7) * mm});
            skLineSegment(sketch, "E15.2.7.3", {"start": v(37.78, -393.7) * mm, "end": v(28.26, -393.7) * mm});
            skLineSegment(sketch, "E15.2.7.4", {"start": v(28.26, -403.23) * mm, "end": v(37.78, -403.23) * mm});
            skLineSegment(sketch, "E15.2.7.5", {"start": v(37.78, -403.22) * mm, "end": v(37.78, -409.57) * mm});
            skLineSegment(sketch, "E15.2.7.6", {"start": v(28.26, -409.57) * mm, "end": v(37.78, -409.57) * mm});
            skLineSegment(sketch, "E15.2.7.7", {"start": v(28.26, -403.22) * mm, "end": v(28.26, -409.57) * mm});
            skLineSegment(sketch, "E15.2.8.0", {"start": v(28.26, -419.1) * mm, "end": v(28.26, -444.5) * mm});
            skLineSegment(sketch, "E15.2.8.1", {"start": v(37.78, -419.1) * mm, "end": v(28.26, -419.1) * mm});
            skLineSegment(sketch, "E15.2.8.2", {"start": v(37.78, -419.1) * mm, "end": v(37.78, -444.5) * mm});
            skLineSegment(sketch, "E15.2.8.3", {"start": v(37.78, -444.5) * mm, "end": v(28.26, -444.5) * mm});
            skLineSegment(sketch, "E15.2.8.4", {"start": v(28.26, -454.03) * mm, "end": v(37.78, -454.03) * mm});
            skLineSegment(sketch, "E15.2.8.5", {"start": v(37.78, -454.02) * mm, "end": v(37.78, -460.38) * mm});
            skLineSegment(sketch, "E15.2.8.6", {"start": v(28.26, -460.38) * mm, "end": v(37.78, -460.38) * mm});
            skLineSegment(sketch, "E15.2.8.7", {"start": v(28.26, -454.02) * mm, "end": v(28.26, -460.38) * mm});
            skLineSegment(sketch, "E15.2.9.0", {"start": v(28.26, -469.9) * mm, "end": v(28.26, -495.3) * mm});
            skLineSegment(sketch, "E15.2.9.1", {"start": v(37.78, -469.9) * mm, "end": v(28.26, -469.9) * mm});
            skLineSegment(sketch, "E15.2.9.2", {"start": v(37.78, -469.9) * mm, "end": v(37.78, -495.3) * mm});
            skLineSegment(sketch, "E15.2.9.3", {"start": v(37.78, -495.3) * mm, "end": v(28.26, -495.3) * mm});
            skLineSegment(sketch, "E15.2.9.4", {"start": v(28.26, -504.82) * mm, "end": v(37.78, -504.82) * mm});
            skLineSegment(sketch, "E15.2.9.5", {"start": v(37.78, -504.82) * mm, "end": v(37.78, -511.17) * mm});
            skLineSegment(sketch, "E15.2.9.6", {"start": v(28.26, -511.18) * mm, "end": v(37.78, -511.18) * mm});
            skLineSegment(sketch, "E15.2.9.7", {"start": v(28.26, -504.82) * mm, "end": v(28.26, -511.17) * mm});
            skLineSegment(sketch, "E15.2.10.0", {"start": v(28.26, -520.7) * mm, "end": v(28.26, -546.1) * mm});
            skLineSegment(sketch, "E15.2.10.1", {"start": v(37.78, -520.7) * mm, "end": v(28.26, -520.7) * mm});
            skLineSegment(sketch, "E15.2.10.2", {"start": v(37.78, -520.7) * mm, "end": v(37.78, -546.1) * mm});
            skLineSegment(sketch, "E15.2.10.3", {"start": v(37.78, -546.1) * mm, "end": v(28.26, -546.1) * mm});
            skLineSegment(sketch, "E15.2.10.4", {"start": v(28.26, -555.62) * mm, "end": v(37.78, -555.62) * mm});
            skLineSegment(sketch, "E15.2.10.5", {"start": v(37.78, -555.62) * mm, "end": v(37.78, -561.98) * mm});
            skLineSegment(sketch, "E15.2.10.6", {"start": v(28.26, -561.98) * mm, "end": v(37.78, -561.98) * mm});
            skLineSegment(sketch, "E15.2.10.7", {"start": v(28.26, -555.62) * mm, "end": v(28.26, -561.98) * mm});
            skLineSegment(sketch, "E15.2.11.0", {"start": v(28.26, -571.5) * mm, "end": v(28.26, -596.9) * mm});
            skLineSegment(sketch, "E15.2.11.1", {"start": v(37.78, -571.5) * mm, "end": v(28.26, -571.5) * mm});
            skLineSegment(sketch, "E15.2.11.2", {"start": v(37.78, -571.5) * mm, "end": v(37.78, -596.9) * mm});
            skLineSegment(sketch, "E15.2.11.3", {"start": v(37.78, -596.9) * mm, "end": v(28.26, -596.9) * mm});
            skLineSegment(sketch, "E15.direction1", {"start": v(66.36, -38.1) * mm, "end": v(47.3, -38.1) * mm, "construction": true});
            skLineSegment(sketch, "E15.direction2", {"start": v(66.36, -38.1) * mm, "end": v(66.36, -88.9) * mm, "construction": true});
            skLineSegment(sketch, "E16.MirrorCS", {"start": v(94.93, -98.43) * mm, "end": v(94.93, -104.78) * mm});
            skLineSegment(sketch, "E17.MirrorCS", {"start": v(94.93, -98.43) * mm, "end": v(85.4, -98.43) * mm});
            skLineSegment(sketch, "E18.MirrorCS", {"start": v(85.4, -241.3) * mm, "end": v(94.93, -241.3) * mm});
            skLineSegment(sketch, "E19.MirrorCS", {"start": v(94.93, -257.18) * mm, "end": v(85.4, -257.18) * mm});
            skLineSegment(sketch, "E20.MirrorCS", {"start": v(85.4, -139.7) * mm, "end": v(94.93, -139.7) * mm});
            skLineSegment(sketch, "E21.MirrorCS", {"start": v(113.98, -555.62) * mm, "end": v(113.98, -561.98) * mm});
            skLineSegment(sketch, "E22.MirrorCS", {"start": v(113.98, -47.63) * mm, "end": v(113.98, -53.98) * mm});
            skLineSegment(sketch, "E23.MirrorCS", {"start": v(94.93, -250.82) * mm, "end": v(94.93, -257.18) * mm});
            skLineSegment(sketch, "E24.MirrorCS", {"start": v(94.93, -149.23) * mm, "end": v(94.93, -155.58) * mm});
            skLineSegment(sketch, "E25.MirrorCS", {"start": v(94.93, -149.22) * mm, "end": v(85.4, -149.22) * mm});
            skLineSegment(sketch, "E26.MirrorCS", {"start": v(85.4, -88.9) * mm, "end": v(94.93, -88.9) * mm});
            skLineSegment(sketch, "E27.MirrorCS", {"start": v(94.93, -104.78) * mm, "end": v(85.4, -104.78) * mm});
            skLineSegment(sketch, "E28.MirrorCS", {"start": v(94.93, -155.58) * mm, "end": v(85.4, -155.58) * mm});
            skLineSegment(sketch, "E29.MirrorCS", {"start": v(94.93, -250.83) * mm, "end": v(85.4, -250.83) * mm});
            skLineSegment(sketch, "E30.MirrorCS", {"start": v(113.98, -257.18) * mm, "end": v(104.46, -257.18) * mm});
            skLineSegment(sketch, "E31.MirrorCS", {"start": v(133.03, -511.18) * mm, "end": v(123.5, -511.18) * mm});
            skLineSegment(sketch, "E32.MirrorCS", {"start": v(113.98, -149.23) * mm, "end": v(113.98, -155.58) * mm});
            skLineSegment(sketch, "E33.MirrorCS", {"start": v(133.03, -98.43) * mm, "end": v(123.5, -98.43) * mm});
            skLineSegment(sketch, "E34.MirrorCS", {"start": v(113.98, -155.58) * mm, "end": v(104.46, -155.58) * mm});
            skLineSegment(sketch, "E35.MirrorCS", {"start": v(113.98, -460.38) * mm, "end": v(104.46, -460.38) * mm});
            skLineSegment(sketch, "E36.MirrorCS", {"start": v(94.93, -403.22) * mm, "end": v(94.93, -409.57) * mm});
            skLineSegment(sketch, "E37.MirrorCS", {"start": v(133.03, -206.37) * mm, "end": v(123.5, -206.37) * mm});
            skLineSegment(sketch, "E38.MirrorCS", {"start": v(123.5, -504.82) * mm, "end": v(123.5, -511.17) * mm});
            skLineSegment(sketch, "E39.MirrorCS", {"start": v(113.98, -555.62) * mm, "end": v(104.46, -555.62) * mm});
            skLineSegment(sketch, "E40.MirrorCS", {"start": v(133.03, -104.78) * mm, "end": v(123.5, -104.78) * mm});
            skLineSegment(sketch, "E41.MirrorCS", {"start": v(133.03, -403.23) * mm, "end": v(123.5, -403.23) * mm});
            skLineSegment(sketch, "E42.MirrorCS", {"start": v(123.5, -403.22) * mm, "end": v(123.5, -409.57) * mm});
            skLineSegment(sketch, "E43.MirrorCS", {"start": v(123.5, -520.7) * mm, "end": v(133.03, -520.7) * mm});
            skLineSegment(sketch, "E44.MirrorCS", {"start": v(94.93, -358.77) * mm, "end": v(85.4, -358.77) * mm});
            skLineSegment(sketch, "E45.MirrorCS", {"start": v(113.98, -206.37) * mm, "end": v(104.46, -206.37) * mm});
            skLineSegment(sketch, "E46.MirrorCS", {"start": v(113.98, -454.02) * mm, "end": v(113.98, -460.38) * mm});
            skLineSegment(sketch, "E47.MirrorCS", {"start": v(113.98, -53.98) * mm, "end": v(104.46, -53.98) * mm});
            skLineSegment(sketch, "E48.MirrorCS", {"start": v(94.93, -460.38) * mm, "end": v(85.4, -460.38) * mm});
            skLineSegment(sketch, "E49.MirrorCS", {"start": v(94.93, -307.98) * mm, "end": v(85.4, -307.98) * mm});
            skLineSegment(sketch, "E50.MirrorCS", {"start": v(113.98, -104.78) * mm, "end": v(104.46, -104.78) * mm});
            skLineSegment(sketch, "E51.MirrorCS", {"start": v(104.46, -38.1) * mm, "end": v(113.98, -38.1) * mm});
            skLineSegment(sketch, "E52.MirrorCS", {"start": v(94.93, -454.02) * mm, "end": v(94.93, -460.38) * mm});
            skLineSegment(sketch, "E53.MirrorCS", {"start": v(113.98, -403.23) * mm, "end": v(104.46, -403.23) * mm});
            skLineSegment(sketch, "E54.MirrorCS", {"start": v(113.98, -301.62) * mm, "end": v(113.98, -307.98) * mm});
            skLineSegment(sketch, "E55.MirrorCS", {"start": v(94.93, -555.62) * mm, "end": v(94.93, -561.98) * mm});
            skLineSegment(sketch, "E56.MirrorCS", {"start": v(94.93, -200.02) * mm, "end": v(85.4, -200.02) * mm});
            skLineSegment(sketch, "E57.MirrorCS", {"start": v(85.4, -469.9) * mm, "end": v(94.93, -469.9) * mm});
            skLineSegment(sketch, "E58.MirrorCS", {"start": v(104.46, -454.02) * mm, "end": v(104.46, -460.38) * mm});
            skLineSegment(sketch, "E59.MirrorCS", {"start": v(94.93, -200.02) * mm, "end": v(94.93, -206.37) * mm});
            skLineSegment(sketch, "E60.MirrorCS", {"start": v(113.98, -403.22) * mm, "end": v(113.98, -409.57) * mm});
            skLineSegment(sketch, "E61.MirrorCS", {"start": v(104.46, -520.7) * mm, "end": v(113.98, -520.7) * mm});
            skLineSegment(sketch, "E62.MirrorCS", {"start": v(113.98, -504.82) * mm, "end": v(104.46, -504.82) * mm});
            skLineSegment(sketch, "E63.MirrorCS", {"start": v(133.03, -504.82) * mm, "end": v(123.5, -504.82) * mm});
            skLineSegment(sketch, "E64.MirrorCS", {"start": v(113.98, -200.02) * mm, "end": v(113.98, -206.37) * mm});
            skLineSegment(sketch, "E65.MirrorCS", {"start": v(104.46, -139.7) * mm, "end": v(113.98, -139.7) * mm});
            skLineSegment(sketch, "E66.MirrorCS", {"start": v(123.5, -301.62) * mm, "end": v(123.5, -307.98) * mm});
            skLineSegment(sketch, "E67.MirrorCS", {"start": v(104.46, -98.43) * mm, "end": v(104.46, -104.78) * mm});
            skLineSegment(sketch, "E68.MirrorCS", {"start": v(94.93, -352.43) * mm, "end": v(85.4, -352.43) * mm});
            skLineSegment(sketch, "E69.MirrorCS", {"start": v(85.4, -38.1) * mm, "end": v(94.93, -38.1) * mm});
            skLineSegment(sketch, "E70.MirrorCS", {"start": v(94.93, -403.23) * mm, "end": v(85.4, -403.23) * mm});
            skLineSegment(sketch, "E71.MirrorCS", {"start": v(85.4, -571.5) * mm, "end": v(94.93, -571.5) * mm});
            skLineSegment(sketch, "E72.MirrorCS", {"start": v(104.46, -301.62) * mm, "end": v(104.46, -307.98) * mm});
            skLineSegment(sketch, "E73.MirrorCS", {"start": v(133.03, -307.98) * mm, "end": v(123.5, -307.98) * mm});
            skLineSegment(sketch, "E74.MirrorCS", {"start": v(94.93, -409.57) * mm, "end": v(85.4, -409.57) * mm});
            skLineSegment(sketch, "E75.MirrorCS", {"start": v(104.46, -47.63) * mm, "end": v(104.46, -53.98) * mm});
            skLineSegment(sketch, "E76.MirrorCS", {"start": v(94.93, -206.37) * mm, "end": v(85.4, -206.37) * mm});
            skLineSegment(sketch, "E77.MirrorCS", {"start": v(104.46, -444.5) * mm, "end": v(113.98, -444.5) * mm});
            skLineSegment(sketch, "E78.MirrorCS", {"start": v(94.93, -555.62) * mm, "end": v(85.4, -555.62) * mm});
            skLineSegment(sketch, "E79.MirrorCS", {"start": v(113.98, -98.43) * mm, "end": v(104.46, -98.43) * mm});
            skLineSegment(sketch, "E80.MirrorCS", {"start": v(113.98, -454.03) * mm, "end": v(104.46, -454.03) * mm});
            skLineSegment(sketch, "E81.MirrorCS", {"start": v(123.5, -419.1) * mm, "end": v(133.03, -419.1) * mm});
            skLineSegment(sketch, "E82.MirrorCS", {"start": v(113.98, -511.18) * mm, "end": v(104.46, -511.18) * mm});
            skLineSegment(sketch, "E83.MirrorCS", {"start": v(123.5, -98.43) * mm, "end": v(123.5, -104.78) * mm});
            skLineSegment(sketch, "E84.MirrorCS", {"start": v(113.98, -307.98) * mm, "end": v(104.46, -307.98) * mm});
            skLineSegment(sketch, "E85.MirrorCS", {"start": v(113.98, -200.02) * mm, "end": v(104.46, -200.02) * mm});
            skLineSegment(sketch, "E86.MirrorCS", {"start": v(104.46, -250.82) * mm, "end": v(104.46, -257.18) * mm});
            skLineSegment(sketch, "E87.MirrorCS", {"start": v(104.46, -200.02) * mm, "end": v(104.46, -206.37) * mm});
            skLineSegment(sketch, "E88.MirrorCS", {"start": v(104.46, -504.82) * mm, "end": v(104.46, -511.17) * mm});
            skLineSegment(sketch, "E89.MirrorCS", {"start": v(133.03, -301.63) * mm, "end": v(123.5, -301.63) * mm});
            skLineSegment(sketch, "E90.MirrorCS", {"start": v(113.98, -352.43) * mm, "end": v(104.46, -352.43) * mm});
            skLineSegment(sketch, "E91.MirrorCS", {"start": v(94.93, -38.1) * mm, "end": v(94.93, -88.9) * mm, "construction": true});
            skLineSegment(sketch, "E92.MirrorCS", {"start": v(94.93, -38.1) * mm, "end": v(113.98, -38.1) * mm, "construction": true});
            skLineSegment(sketch, "E93.MirrorCS", {"start": v(94.93, -504.82) * mm, "end": v(85.4, -504.82) * mm});
            skLineSegment(sketch, "E94.MirrorCS", {"start": v(113.98, -358.77) * mm, "end": v(104.46, -358.77) * mm});
            skLineSegment(sketch, "E95.MirrorCS", {"start": v(113.98, -47.63) * mm, "end": v(104.46, -47.63) * mm});
            skLineSegment(sketch, "E96.MirrorCS", {"start": v(94.93, -511.18) * mm, "end": v(85.4, -511.18) * mm});
            skLineSegment(sketch, "E97.MirrorCS", {"start": v(113.98, -504.82) * mm, "end": v(113.98, -511.17) * mm});
            skLineSegment(sketch, "E98.MirrorCS", {"start": v(104.46, -88.9) * mm, "end": v(113.98, -88.9) * mm});
            skLineSegment(sketch, "E99.MirrorCS", {"start": v(104.46, -241.3) * mm, "end": v(113.98, -241.3) * mm});
            skLineSegment(sketch, "E100.MirrorCS", {"start": v(113.98, -561.98) * mm, "end": v(104.46, -561.98) * mm});
            skLineSegment(sketch, "E101.MirrorCS", {"start": v(133.03, -200.02) * mm, "end": v(123.5, -200.02) * mm});
            skLineSegment(sketch, "E102.MirrorCS", {"start": v(104.46, -342.9) * mm, "end": v(113.98, -342.9) * mm});
            skLineSegment(sketch, "E103.MirrorCS", {"start": v(133.03, -409.57) * mm, "end": v(123.5, -409.57) * mm});
            skLineSegment(sketch, "E104.MirrorCS", {"start": v(94.93, -352.42) * mm, "end": v(94.93, -358.77) * mm});
            skLineSegment(sketch, "E105.MirrorCS", {"start": v(104.46, -419.1) * mm, "end": v(113.98, -419.1) * mm});
            skLineSegment(sketch, "E106.MirrorCS", {"start": v(123.5, -190.5) * mm, "end": v(133.03, -190.5) * mm});
            skLineSegment(sketch, "E107.MirrorCS", {"start": v(113.98, -301.63) * mm, "end": v(104.46, -301.63) * mm});
            skLineSegment(sketch, "E108.MirrorCS", {"start": v(104.46, -546.1) * mm, "end": v(113.98, -546.1) * mm});
            skLineSegment(sketch, "E109.MirrorCS", {"start": v(123.5, -200.02) * mm, "end": v(123.5, -206.37) * mm});
            skLineSegment(sketch, "E110.MirrorCS", {"start": v(113.98, -250.82) * mm, "end": v(113.98, -257.18) * mm});
            skLineSegment(sketch, "E111.MirrorCS", {"start": v(94.93, -301.62) * mm, "end": v(94.93, -307.98) * mm});
            skLineSegment(sketch, "E112.MirrorCS", {"start": v(94.93, -561.98) * mm, "end": v(85.4, -561.98) * mm});
            skLineSegment(sketch, "E113.MirrorCS", {"start": v(104.46, -555.62) * mm, "end": v(104.46, -561.98) * mm});
            skLineSegment(sketch, "E114.MirrorCS", {"start": v(113.98, -98.43) * mm, "end": v(113.98, -104.78) * mm});
            skLineSegment(sketch, "E115.MirrorCS", {"start": v(94.93, -301.63) * mm, "end": v(85.4, -301.63) * mm});
            skLineSegment(sketch, "E116.MirrorCS", {"start": v(104.46, -352.42) * mm, "end": v(104.46, -358.77) * mm});
            skLineSegment(sketch, "E117.MirrorCS", {"start": v(85.4, -520.7) * mm, "end": v(94.93, -520.7) * mm});
            skLineSegment(sketch, "E118.MirrorCS", {"start": v(94.93, -454.03) * mm, "end": v(85.4, -454.03) * mm});
            skLineSegment(sketch, "E119.MirrorCS", {"start": v(123.5, -88.9) * mm, "end": v(133.03, -88.9) * mm});
            skLineSegment(sketch, "E120.MirrorCS", {"start": v(104.46, -149.23) * mm, "end": v(104.46, -155.58) * mm});
            skLineSegment(sketch, "E121.MirrorCS", {"start": v(113.98, -352.42) * mm, "end": v(113.98, -358.77) * mm});
            skLineSegment(sketch, "E122.MirrorCS", {"start": v(113.98, -409.57) * mm, "end": v(104.46, -409.57) * mm});
            skLineSegment(sketch, "E123.MirrorCS", {"start": v(113.98, -250.83) * mm, "end": v(104.46, -250.83) * mm});
            skLineSegment(sketch, "E124.MirrorCS", {"start": v(85.4, -190.5) * mm, "end": v(94.93, -190.5) * mm});
            skLineSegment(sketch, "E125.MirrorCS", {"start": v(94.93, -504.82) * mm, "end": v(94.93, -511.17) * mm});
            skLineSegment(sketch, "E126.MirrorCS", {"start": v(104.46, -403.22) * mm, "end": v(104.46, -409.57) * mm});
            skLineSegment(sketch, "E127.MirrorCS", {"start": v(113.98, -149.22) * mm, "end": v(104.46, -149.22) * mm});
            skLineSegment(sketch, "E128.MirrorCS", {"start": v(104.46, -596.9) * mm, "end": v(113.98, -596.9) * mm});
            skLineSegment(sketch, "E129.MirrorCS", {"start": v(104.46, -165.1) * mm, "end": v(113.98, -165.1) * mm});
            skLineSegment(sketch, "E130.MirrorCS", {"start": v(123.5, -114.3) * mm, "end": v(133.03, -114.3) * mm});
            skLineSegment(sketch, "E131.MirrorCS", {"start": v(94.93, -47.63) * mm, "end": v(94.93, -53.98) * mm});
            skLineSegment(sketch, "E132.MirrorCS", {"start": v(133.03, -454.03) * mm, "end": v(123.5, -454.03) * mm});
            skLineSegment(sketch, "E133.MirrorCS", {"start": v(133.03, -504.82) * mm, "end": v(133.03, -511.17) * mm});
            skLineSegment(sketch, "E134.MirrorCS", {"start": v(123.5, -495.3) * mm, "end": v(133.03, -495.3) * mm});
            skLineSegment(sketch, "E135.MirrorCS", {"start": v(123.5, -149.23) * mm, "end": v(123.5, -155.58) * mm});
            skLineSegment(sketch, "E136.MirrorCS", {"start": v(85.4, -444.5) * mm, "end": v(94.93, -444.5) * mm});
            skLineSegment(sketch, "E137.MirrorCS", {"start": v(85.4, -250.82) * mm, "end": v(85.4, -257.18) * mm});
            skLineSegment(sketch, "E138.MirrorCS", {"start": v(123.5, -241.3) * mm, "end": v(133.03, -241.3) * mm});
            skLineSegment(sketch, "E139.MirrorCS", {"start": v(133.03, -301.62) * mm, "end": v(133.03, -307.98) * mm});
            skLineSegment(sketch, "E140.MirrorCS", {"start": v(133.03, -555.62) * mm, "end": v(123.5, -555.62) * mm});
            skLineSegment(sketch, "E141.MirrorCS", {"start": v(104.46, -215.9) * mm, "end": v(113.98, -215.9) * mm});
            skLineSegment(sketch, "E142.MirrorCS", {"start": v(133.03, -257.18) * mm, "end": v(123.5, -257.18) * mm});
            skLineSegment(sketch, "E143.MirrorCS", {"start": v(123.5, -454.02) * mm, "end": v(123.5, -460.38) * mm});
            skLineSegment(sketch, "E144.MirrorCS", {"start": v(123.5, -139.7) * mm, "end": v(133.03, -139.7) * mm});
            skLineSegment(sketch, "E145.MirrorCS", {"start": v(133.03, -98.43) * mm, "end": v(133.03, -104.78) * mm});
            skLineSegment(sketch, "E146.MirrorCS", {"start": v(133.03, -561.98) * mm, "end": v(123.5, -561.98) * mm});
            skLineSegment(sketch, "E147.MirrorCS", {"start": v(133.03, -403.22) * mm, "end": v(133.03, -409.57) * mm});
            skLineSegment(sketch, "E148.MirrorCS", {"start": v(133.03, -352.42) * mm, "end": v(133.03, -358.77) * mm});
            skLineSegment(sketch, "E149.MirrorCS", {"start": v(133.03, -47.63) * mm, "end": v(123.5, -47.63) * mm});
            skLineSegment(sketch, "E150.MirrorCS", {"start": v(104.46, -266.7) * mm, "end": v(113.98, -266.7) * mm});
            skLineSegment(sketch, "E151.MirrorCS", {"start": v(123.5, -469.9) * mm, "end": v(133.03, -469.9) * mm});
            skLineSegment(sketch, "E152.MirrorCS", {"start": v(104.46, -571.5) * mm, "end": v(113.98, -571.5) * mm});
            skLineSegment(sketch, "E153.MirrorCS", {"start": v(123.5, -292.1) * mm, "end": v(133.03, -292.1) * mm});
            skLineSegment(sketch, "E154.MirrorCS", {"start": v(104.46, -393.7) * mm, "end": v(113.98, -393.7) * mm});
            skLineSegment(sketch, "E155.MirrorCS", {"start": v(133.03, -149.22) * mm, "end": v(123.5, -149.22) * mm});
            skLineSegment(sketch, "E156.MirrorCS", {"start": v(133.03, -352.43) * mm, "end": v(123.5, -352.43) * mm});
            skLineSegment(sketch, "E157.MirrorCS", {"start": v(85.4, -317.5) * mm, "end": v(94.93, -317.5) * mm});
            skLineSegment(sketch, "E158.MirrorCS", {"start": v(133.03, -53.98) * mm, "end": v(123.5, -53.98) * mm});
            skLineSegment(sketch, "E159.MirrorCS", {"start": v(104.46, -469.9) * mm, "end": v(113.98, -469.9) * mm});
            skLineSegment(sketch, "E160.MirrorCS", {"start": v(85.4, -352.42) * mm, "end": v(85.4, -358.77) * mm});
            skLineSegment(sketch, "E161.MirrorCS", {"start": v(123.5, -12.7) * mm, "end": v(133.03, -12.7) * mm});
            skLineSegment(sketch, "E162.MirrorCS", {"start": v(94.93, -47.63) * mm, "end": v(85.4, -47.63) * mm});
            skLineSegment(sketch, "E163.MirrorCS", {"start": v(104.46, -317.5) * mm, "end": v(113.98, -317.5) * mm});
            skLineSegment(sketch, "E164.MirrorCS", {"start": v(85.4, -546.1) * mm, "end": v(94.93, -546.1) * mm});
            skLineSegment(sketch, "E165.MirrorCS", {"start": v(123.5, -38.1) * mm, "end": v(133.03, -38.1) * mm});
            skLineSegment(sketch, "E166.MirrorCS", {"start": v(85.4, -555.62) * mm, "end": v(85.4, -561.98) * mm});
            skLineSegment(sketch, "E167.MirrorCS", {"start": v(133.03, -460.38) * mm, "end": v(123.5, -460.38) * mm});
            skLineSegment(sketch, "E168.MirrorCS", {"start": v(104.46, -114.3) * mm, "end": v(113.98, -114.3) * mm});
            skLineSegment(sketch, "E169.MirrorCS", {"start": v(104.46, -12.7) * mm, "end": v(113.98, -12.7) * mm});
            skLineSegment(sketch, "E170.MirrorCS", {"start": v(123.5, -444.5) * mm, "end": v(133.03, -444.5) * mm});
            skLineSegment(sketch, "E171.MirrorCS", {"start": v(104.46, -368.3) * mm, "end": v(113.98, -368.3) * mm});
            skLineSegment(sketch, "E172.MirrorCS", {"start": v(123.5, -555.62) * mm, "end": v(123.5, -561.98) * mm});
            skLineSegment(sketch, "E173.MirrorCS", {"start": v(123.5, -546.1) * mm, "end": v(133.03, -546.1) * mm});
            skLineSegment(sketch, "E174.MirrorCS", {"start": v(104.46, -63.5) * mm, "end": v(113.98, -63.5) * mm});
            skLineSegment(sketch, "E175.MirrorCS", {"start": v(85.4, -98.43) * mm, "end": v(85.4, -104.78) * mm});
            skLineSegment(sketch, "E176.MirrorCS", {"start": v(133.03, -250.83) * mm, "end": v(123.5, -250.83) * mm});
            skLineSegment(sketch, "E177.MirrorCS", {"start": v(123.5, -47.63) * mm, "end": v(123.5, -53.98) * mm});
            skLineSegment(sketch, "E178.MirrorCS", {"start": v(123.5, -317.5) * mm, "end": v(133.03, -317.5) * mm});
            skLineSegment(sketch, "E179.MirrorCS", {"start": v(85.4, -114.3) * mm, "end": v(94.93, -114.3) * mm});
            skLineSegment(sketch, "E180.MirrorCS", {"start": v(85.4, -419.1) * mm, "end": v(94.93, -419.1) * mm});
            skLineSegment(sketch, "E181.MirrorCS", {"start": v(133.03, -358.77) * mm, "end": v(123.5, -358.77) * mm});
            skLineSegment(sketch, "E182.MirrorCS", {"start": v(123.5, -596.9) * mm, "end": v(133.03, -596.9) * mm});
            skLineSegment(sketch, "E183.MirrorCS", {"start": v(85.4, -149.23) * mm, "end": v(85.4, -155.58) * mm});
            skLineSegment(sketch, "E184.MirrorCS", {"start": v(94.93, -53.98) * mm, "end": v(85.4, -53.98) * mm});
            skLineSegment(sketch, "E185.MirrorCS", {"start": v(133.03, -200.02) * mm, "end": v(133.03, -206.37) * mm});
            skLineSegment(sketch, "E186.MirrorCS", {"start": v(85.4, -454.02) * mm, "end": v(85.4, -460.38) * mm});
            skLineSegment(sketch, "E187.MirrorCS", {"start": v(104.46, -292.1) * mm, "end": v(113.98, -292.1) * mm});
            skLineSegment(sketch, "E188.MirrorCS", {"start": v(123.5, -63.5) * mm, "end": v(133.03, -63.5) * mm});
            skLineSegment(sketch, "E189.MirrorCS", {"start": v(85.4, -63.5) * mm, "end": v(94.93, -63.5) * mm});
            skLineSegment(sketch, "E190.MirrorCS", {"start": v(133.03, -454.02) * mm, "end": v(133.03, -460.38) * mm});
            skLineSegment(sketch, "E191.MirrorCS", {"start": v(133.03, -149.23) * mm, "end": v(133.03, -155.58) * mm});
            skLineSegment(sketch, "E192.MirrorCS", {"start": v(104.46, -190.5) * mm, "end": v(113.98, -190.5) * mm});
            skLineSegment(sketch, "E193.MirrorCS", {"start": v(123.5, -352.42) * mm, "end": v(123.5, -358.77) * mm});
            skLineSegment(sketch, "E194.MirrorCS", {"start": v(133.03, -155.58) * mm, "end": v(123.5, -155.58) * mm});
            skLineSegment(sketch, "E195.MirrorCS", {"start": v(133.03, -47.63) * mm, "end": v(133.03, -53.98) * mm});
            skLineSegment(sketch, "E196.MirrorCS", {"start": v(123.5, -393.7) * mm, "end": v(133.03, -393.7) * mm});
            skLineSegment(sketch, "E197.MirrorCS", {"start": v(133.03, -250.82) * mm, "end": v(133.03, -257.18) * mm});
            skLineSegment(sketch, "E198.MirrorCS", {"start": v(123.5, -342.9) * mm, "end": v(133.03, -342.9) * mm});
            skLineSegment(sketch, "E199.MirrorCS", {"start": v(85.4, -342.9) * mm, "end": v(94.93, -342.9) * mm});
            skLineSegment(sketch, "E200.MirrorCS", {"start": v(123.5, -571.5) * mm, "end": v(133.03, -571.5) * mm});
            skLineSegment(sketch, "E201.MirrorCS", {"start": v(123.5, -215.9) * mm, "end": v(133.03, -215.9) * mm});
            skLineSegment(sketch, "E202.MirrorCS", {"start": v(133.03, -555.62) * mm, "end": v(133.03, -561.98) * mm});
            skLineSegment(sketch, "E203.MirrorCS", {"start": v(104.46, -495.3) * mm, "end": v(113.98, -495.3) * mm});
            skLineSegment(sketch, "E204.MirrorCS", {"start": v(123.5, -250.82) * mm, "end": v(123.5, -257.18) * mm});
            skLineSegment(sketch, "E205.MirrorCS", {"start": v(85.4, -215.9) * mm, "end": v(94.93, -215.9) * mm});
            skLineSegment(sketch, "E206.MirrorCS", {"start": v(85.4, -596.9) * mm, "end": v(94.93, -596.9) * mm});
            skLineSegment(sketch, "E207.MirrorCS", {"start": v(85.4, -165.1) * mm, "end": v(94.93, -165.1) * mm});
            skLineSegment(sketch, "E208.MirrorCS", {"start": v(85.4, -12.7) * mm, "end": v(94.93, -12.7) * mm});
            skLineSegment(sketch, "E209.MirrorCS", {"start": v(123.5, -368.3) * mm, "end": v(133.03, -368.3) * mm});
            skLineSegment(sketch, "E210.MirrorCS", {"start": v(85.4, -403.22) * mm, "end": v(85.4, -409.57) * mm});
            skLineSegment(sketch, "E211.MirrorCS", {"start": v(85.4, -504.82) * mm, "end": v(85.4, -511.17) * mm});
            skLineSegment(sketch, "E212.MirrorCS", {"start": v(123.5, -266.7) * mm, "end": v(133.03, -266.7) * mm});
            skLineSegment(sketch, "E213.MirrorCS", {"start": v(85.4, -495.3) * mm, "end": v(94.93, -495.3) * mm});
            skLineSegment(sketch, "E214.MirrorCS", {"start": v(85.4, -301.62) * mm, "end": v(85.4, -307.98) * mm});
            skLineSegment(sketch, "E215.MirrorCS", {"start": v(85.4, -200.02) * mm, "end": v(85.4, -206.37) * mm});
            skLineSegment(sketch, "E216.MirrorCS", {"start": v(85.4, -266.7) * mm, "end": v(94.93, -266.7) * mm});
            skLineSegment(sketch, "E217.MirrorCS", {"start": v(85.4, -292.1) * mm, "end": v(94.93, -292.1) * mm});
            skLineSegment(sketch, "E218.MirrorCS", {"start": v(85.4, -393.7) * mm, "end": v(94.93, -393.7) * mm});
            skLineSegment(sketch, "E219.MirrorCS", {"start": v(85.4, -47.63) * mm, "end": v(85.4, -53.98) * mm});
            skLineSegment(sketch, "E220.MirrorCS", {"start": v(123.5, -165.1) * mm, "end": v(133.03, -165.1) * mm});
            skLineSegment(sketch, "E221.MirrorCS", {"start": v(85.4, -368.3) * mm, "end": v(94.93, -368.3) * mm});
            skLineSegment(sketch, "E222.MirrorCS", {"start": v(94.93, -63.5) * mm, "end": v(94.93, -88.9) * mm});
            skLineSegment(sketch, "E223.MirrorCS", {"start": v(133.03, -419.1) * mm, "end": v(133.03, -444.5) * mm});
            skLineSegment(sketch, "E224.MirrorCS", {"start": v(133.03, -114.3) * mm, "end": v(133.03, -139.7) * mm});
            skLineSegment(sketch, "E225.MirrorCS", {"start": v(104.46, -165.1) * mm, "end": v(104.46, -190.5) * mm});
            skLineSegment(sketch, "E226.MirrorCS", {"start": v(123.5, -317.5) * mm, "end": v(123.5, -342.9) * mm});
            skLineSegment(sketch, "E227.MirrorCS", {"start": v(104.46, -266.7) * mm, "end": v(104.46, -292.1) * mm});
            skLineSegment(sketch, "E228.MirrorCS", {"start": v(104.46, -520.7) * mm, "end": v(104.46, -546.1) * mm});
            skLineSegment(sketch, "E229.MirrorCS", {"start": v(123.5, -469.9) * mm, "end": v(123.5, -495.3) * mm});
            skLineSegment(sketch, "E230.MirrorCS", {"start": v(123.5, -419.1) * mm, "end": v(123.5, -444.5) * mm});
            skLineSegment(sketch, "E231.MirrorCS", {"start": v(123.5, -266.7) * mm, "end": v(123.5, -292.1) * mm});
            skLineSegment(sketch, "E232.MirrorCS", {"start": v(85.4, -469.9) * mm, "end": v(85.4, -495.3) * mm});
            skLineSegment(sketch, "E233.MirrorCS", {"start": v(113.98, -571.5) * mm, "end": v(113.98, -596.9) * mm});
            skLineSegment(sketch, "E234.MirrorCS", {"start": v(123.5, -114.3) * mm, "end": v(123.5, -139.7) * mm});
            skLineSegment(sketch, "E235.MirrorCS", {"start": v(85.4, -114.3) * mm, "end": v(85.4, -139.7) * mm});
            skLineSegment(sketch, "E236.MirrorCS", {"start": v(133.03, -469.9) * mm, "end": v(133.03, -495.3) * mm});
            skLineSegment(sketch, "E237.MirrorCS", {"start": v(113.98, -165.1) * mm, "end": v(113.98, -190.5) * mm});
            skLineSegment(sketch, "E238.MirrorCS", {"start": v(94.93, -520.7) * mm, "end": v(94.93, -546.1) * mm});
            skLineSegment(sketch, "E239.MirrorCS", {"start": v(104.46, -12.7) * mm, "end": v(104.46, -38.1) * mm});
            skLineSegment(sketch, "E240.MirrorCS", {"start": v(85.4, -165.1) * mm, "end": v(85.4, -190.5) * mm});
            skLineSegment(sketch, "E241.MirrorCS", {"start": v(85.4, -520.7) * mm, "end": v(85.4, -546.1) * mm});
            skLineSegment(sketch, "E242.MirrorCS", {"start": v(113.98, -520.7) * mm, "end": v(113.98, -546.1) * mm});
            skLineSegment(sketch, "E243.MirrorCS", {"start": v(113.98, -63.5) * mm, "end": v(113.98, -88.9) * mm});
            skLineSegment(sketch, "E244.MirrorCS", {"start": v(123.5, -368.3) * mm, "end": v(123.5, -393.7) * mm});
            skLineSegment(sketch, "E245.MirrorCS", {"start": v(85.4, -571.5) * mm, "end": v(85.4, -596.9) * mm});
            skLineSegment(sketch, "E246.MirrorCS", {"start": v(113.98, -266.7) * mm, "end": v(113.98, -292.1) * mm});
            skLineSegment(sketch, "E247.MirrorCS", {"start": v(123.5, -12.7) * mm, "end": v(123.5, -38.1) * mm});
            skLineSegment(sketch, "E248.MirrorCS", {"start": v(85.4, -63.5) * mm, "end": v(85.4, -88.9) * mm});
            skLineSegment(sketch, "E249.MirrorCS", {"start": v(133.03, -165.1) * mm, "end": v(133.03, -190.5) * mm});
            skLineSegment(sketch, "E250.MirrorCS", {"start": v(113.98, -469.9) * mm, "end": v(113.98, -495.3) * mm});
            skLineSegment(sketch, "E251.MirrorCS", {"start": v(133.03, -368.3) * mm, "end": v(133.03, -393.7) * mm});
            skLineSegment(sketch, "E252.MirrorCS", {"start": v(113.98, -368.3) * mm, "end": v(113.98, -393.7) * mm});
            skLineSegment(sketch, "E253.MirrorCS", {"start": v(133.03, -520.7) * mm, "end": v(133.03, -546.1) * mm});
            skLineSegment(sketch, "E254.MirrorCS", {"start": v(85.4, -215.9) * mm, "end": v(85.4, -241.3) * mm});
            skLineSegment(sketch, "E255.MirrorCS", {"start": v(85.4, -266.7) * mm, "end": v(85.4, -292.1) * mm});
            skLineSegment(sketch, "E256.MirrorCS", {"start": v(85.4, -419.1) * mm, "end": v(85.4, -444.5) * mm});
            skLineSegment(sketch, "E257.MirrorCS", {"start": v(123.5, -520.7) * mm, "end": v(123.5, -546.1) * mm});
            skLineSegment(sketch, "E258.MirrorCS", {"start": v(94.93, -215.9) * mm, "end": v(94.93, -241.3) * mm});
            skLineSegment(sketch, "E259.MirrorCS", {"start": v(113.98, -12.7) * mm, "end": v(113.98, -38.1) * mm});
            skLineSegment(sketch, "E260.MirrorCS", {"start": v(113.98, -419.1) * mm, "end": v(113.98, -444.5) * mm});
            skLineSegment(sketch, "E261.MirrorCS", {"start": v(94.93, -419.1) * mm, "end": v(94.93, -444.5) * mm});
            skLineSegment(sketch, "E262.MirrorCS", {"start": v(94.93, -571.5) * mm, "end": v(94.93, -596.9) * mm});
            skLineSegment(sketch, "E263.MirrorCS", {"start": v(85.4, -317.5) * mm, "end": v(85.4, -342.9) * mm});
            skLineSegment(sketch, "E264.MirrorCS", {"start": v(123.5, -165.1) * mm, "end": v(123.5, -190.5) * mm});
            skLineSegment(sketch, "E265.MirrorCS", {"start": v(85.4, -368.3) * mm, "end": v(85.4, -393.7) * mm});
            skLineSegment(sketch, "E266.MirrorCS", {"start": v(104.46, -368.3) * mm, "end": v(104.46, -393.7) * mm});
            skLineSegment(sketch, "E267.MirrorCS", {"start": v(113.98, -114.3) * mm, "end": v(113.98, -139.7) * mm});
            skLineSegment(sketch, "E268.MirrorCS", {"start": v(104.46, -63.5) * mm, "end": v(104.46, -88.9) * mm});
            skLineSegment(sketch, "E269.MirrorCS", {"start": v(94.93, -317.5) * mm, "end": v(94.93, -342.9) * mm});
            skLineSegment(sketch, "E270.MirrorCS", {"start": v(94.93, -469.9) * mm, "end": v(94.93, -495.3) * mm});
            skLineSegment(sketch, "E271.MirrorCS", {"start": v(133.03, -571.5) * mm, "end": v(133.03, -596.9) * mm});
            skLineSegment(sketch, "E272.MirrorCS", {"start": v(104.46, -215.9) * mm, "end": v(104.46, -241.3) * mm});
            skLineSegment(sketch, "E273.MirrorCS", {"start": v(113.98, -215.9) * mm, "end": v(113.98, -241.3) * mm});
            skLineSegment(sketch, "E274.MirrorCS", {"start": v(133.03, -12.7) * mm, "end": v(133.03, -38.1) * mm});
            skLineSegment(sketch, "E275.MirrorCS", {"start": v(104.46, -469.9) * mm, "end": v(104.46, -495.3) * mm});
            skLineSegment(sketch, "E276.MirrorCS", {"start": v(94.93, -165.1) * mm, "end": v(94.93, -190.5) * mm});
            skLineSegment(sketch, "E277.MirrorCS", {"start": v(94.93, -114.3) * mm, "end": v(94.93, -139.7) * mm});
            skLineSegment(sketch, "E278.MirrorCS", {"start": v(94.93, -368.3) * mm, "end": v(94.93, -393.7) * mm});
            skLineSegment(sketch, "E279.MirrorCS", {"start": v(104.46, -571.5) * mm, "end": v(104.46, -596.9) * mm});
            skLineSegment(sketch, "E280.MirrorCS", {"start": v(123.5, -571.5) * mm, "end": v(123.5, -596.9) * mm});
            skLineSegment(sketch, "E281.MirrorCS", {"start": v(104.46, -317.5) * mm, "end": v(104.46, -342.9) * mm});
            skLineSegment(sketch, "E282.MirrorCS", {"start": v(85.4, -12.7) * mm, "end": v(85.4, -38.1) * mm});
            skLineSegment(sketch, "E283.MirrorCS", {"start": v(113.98, -317.5) * mm, "end": v(113.98, -342.9) * mm});
            skLineSegment(sketch, "E284.MirrorCS", {"start": v(133.03, -317.5) * mm, "end": v(133.03, -342.9) * mm});
            skLineSegment(sketch, "E285.MirrorCS", {"start": v(133.03, -266.7) * mm, "end": v(133.03, -292.1) * mm});
            skLineSegment(sketch, "E286.MirrorCS", {"start": v(133.03, -63.5) * mm, "end": v(133.03, -88.9) * mm});
            skLineSegment(sketch, "E287.MirrorCS", {"start": v(94.93, -12.7) * mm, "end": v(94.93, -38.1) * mm});
            skLineSegment(sketch, "E288.MirrorCS", {"start": v(133.03, -215.9) * mm, "end": v(133.03, -241.3) * mm});
            skLineSegment(sketch, "E289.MirrorCS", {"start": v(94.93, -266.7) * mm, "end": v(94.93, -292.1) * mm});
            skLineSegment(sketch, "E290.MirrorCS", {"start": v(104.46, -419.1) * mm, "end": v(104.46, -444.5) * mm});
            skLineSegment(sketch, "E291.MirrorCS", {"start": v(123.5, -215.9) * mm, "end": v(123.5, -241.3) * mm});
            skLineSegment(sketch, "E292.MirrorCS", {"start": v(104.46, -114.3) * mm, "end": v(104.46, -139.7) * mm});
            skLineSegment(sketch, "E293.MirrorCS", {"start": v(123.5, -63.5) * mm, "end": v(123.5, -88.9) * mm});
            skLineSegment(sketch, "E294.0.3.0", {"start": v(9.2, -12.7) * mm, "end": v(9.2, -38.1) * mm});
            skLineSegment(sketch, "E294.3.3.0", {"start": v(18.73, -12.7) * mm, "end": v(9.2, -12.7) * mm});
            skLineSegment(sketch, "E294.6.3.0", {"start": v(18.73, -12.7) * mm, "end": v(18.73, -38.1) * mm});
            skLineSegment(sketch, "E294.9.3.0", {"start": v(18.73, -38.1) * mm, "end": v(9.2, -38.1) * mm});
            skLineSegment(sketch, "E294.12.3.0", {"start": v(9.2, -47.63) * mm, "end": v(18.73, -47.63) * mm});
            skLineSegment(sketch, "E294.15.3.0", {"start": v(18.73, -47.63) * mm, "end": v(18.73, -53.98) * mm});
            skLineSegment(sketch, "E294.18.3.0", {"start": v(9.2, -53.98) * mm, "end": v(18.73, -53.98) * mm});
            skLineSegment(sketch, "E294.21.3.0", {"start": v(9.2, -47.63) * mm, "end": v(9.2, -53.98) * mm});
            skLineSegment(sketch, "E294.0.3.1", {"start": v(9.2, -63.5) * mm, "end": v(9.2, -88.9) * mm});
            skLineSegment(sketch, "E294.3.3.1", {"start": v(18.73, -63.5) * mm, "end": v(9.2, -63.5) * mm});
            skLineSegment(sketch, "E294.6.3.1", {"start": v(18.73, -63.5) * mm, "end": v(18.73, -88.9) * mm});
            skLineSegment(sketch, "E294.9.3.1", {"start": v(18.73, -88.9) * mm, "end": v(9.2, -88.9) * mm});
            skLineSegment(sketch, "E294.12.3.1", {"start": v(9.2, -98.43) * mm, "end": v(18.73, -98.43) * mm});
            skLineSegment(sketch, "E294.15.3.1", {"start": v(18.73, -98.43) * mm, "end": v(18.73, -104.78) * mm});
            skLineSegment(sketch, "E294.18.3.1", {"start": v(9.2, -104.78) * mm, "end": v(18.73, -104.78) * mm});
            skLineSegment(sketch, "E294.21.3.1", {"start": v(9.2, -98.43) * mm, "end": v(9.2, -104.78) * mm});
            skLineSegment(sketch, "E294.0.3.2", {"start": v(9.2, -114.3) * mm, "end": v(9.2, -139.7) * mm});
            skLineSegment(sketch, "E294.3.3.2", {"start": v(18.73, -114.3) * mm, "end": v(9.2, -114.3) * mm});
            skLineSegment(sketch, "E294.6.3.2", {"start": v(18.73, -114.3) * mm, "end": v(18.73, -139.7) * mm});
            skLineSegment(sketch, "E294.9.3.2", {"start": v(18.73, -139.7) * mm, "end": v(9.2, -139.7) * mm});
            skLineSegment(sketch, "E294.12.3.2", {"start": v(9.2, -149.22) * mm, "end": v(18.73, -149.22) * mm});
            skLineSegment(sketch, "E294.15.3.2", {"start": v(18.73, -149.22) * mm, "end": v(18.73, -155.58) * mm});
            skLineSegment(sketch, "E294.18.3.2", {"start": v(9.2, -155.58) * mm, "end": v(18.73, -155.58) * mm});
            skLineSegment(sketch, "E294.21.3.2", {"start": v(9.2, -149.22) * mm, "end": v(9.2, -155.58) * mm});
            skLineSegment(sketch, "E294.0.3.3", {"start": v(9.2, -165.1) * mm, "end": v(9.2, -190.5) * mm});
            skLineSegment(sketch, "E294.3.3.3", {"start": v(18.73, -165.1) * mm, "end": v(9.2, -165.1) * mm});
            skLineSegment(sketch, "E294.6.3.3", {"start": v(18.73, -165.1) * mm, "end": v(18.73, -190.5) * mm});
            skLineSegment(sketch, "E294.9.3.3", {"start": v(18.73, -190.5) * mm, "end": v(9.2, -190.5) * mm});
            skLineSegment(sketch, "E294.12.3.3", {"start": v(9.2, -200.02) * mm, "end": v(18.73, -200.02) * mm});
            skLineSegment(sketch, "E294.15.3.3", {"start": v(18.73, -200.02) * mm, "end": v(18.73, -206.37) * mm});
            skLineSegment(sketch, "E294.18.3.3", {"start": v(9.2, -206.37) * mm, "end": v(18.73, -206.37) * mm});
            skLineSegment(sketch, "E294.21.3.3", {"start": v(9.2, -200.02) * mm, "end": v(9.2, -206.37) * mm});
            skLineSegment(sketch, "E294.0.3.4", {"start": v(9.2, -215.9) * mm, "end": v(9.2, -241.3) * mm});
            skLineSegment(sketch, "E294.3.3.4", {"start": v(18.73, -215.9) * mm, "end": v(9.2, -215.9) * mm});
            skLineSegment(sketch, "E294.6.3.4", {"start": v(18.73, -215.9) * mm, "end": v(18.73, -241.3) * mm});
            skLineSegment(sketch, "E294.9.3.4", {"start": v(18.73, -241.3) * mm, "end": v(9.2, -241.3) * mm});
            skLineSegment(sketch, "E294.12.3.4", {"start": v(9.2, -250.83) * mm, "end": v(18.73, -250.83) * mm});
            skLineSegment(sketch, "E294.15.3.4", {"start": v(18.73, -250.83) * mm, "end": v(18.73, -257.18) * mm});
            skLineSegment(sketch, "E294.18.3.4", {"start": v(9.2, -257.18) * mm, "end": v(18.73, -257.18) * mm});
            skLineSegment(sketch, "E294.21.3.4", {"start": v(9.2, -250.83) * mm, "end": v(9.2, -257.18) * mm});
            skLineSegment(sketch, "E294.0.3.5", {"start": v(9.2, -266.7) * mm, "end": v(9.2, -292.1) * mm});
            skLineSegment(sketch, "E294.3.3.5", {"start": v(18.73, -266.7) * mm, "end": v(9.2, -266.7) * mm});
            skLineSegment(sketch, "E294.6.3.5", {"start": v(18.73, -266.7) * mm, "end": v(18.73, -292.1) * mm});
            skLineSegment(sketch, "E294.9.3.5", {"start": v(18.73, -292.1) * mm, "end": v(9.2, -292.1) * mm});
            skLineSegment(sketch, "E294.12.3.5", {"start": v(9.2, -301.63) * mm, "end": v(18.73, -301.63) * mm});
            skLineSegment(sketch, "E294.15.3.5", {"start": v(18.73, -301.63) * mm, "end": v(18.73, -307.98) * mm});
            skLineSegment(sketch, "E294.18.3.5", {"start": v(9.2, -307.98) * mm, "end": v(18.73, -307.98) * mm});
            skLineSegment(sketch, "E294.21.3.5", {"start": v(9.2, -301.63) * mm, "end": v(9.2, -307.98) * mm});
            skLineSegment(sketch, "E294.0.3.6", {"start": v(9.2, -317.5) * mm, "end": v(9.2, -342.9) * mm});
            skLineSegment(sketch, "E294.3.3.6", {"start": v(18.73, -317.5) * mm, "end": v(9.2, -317.5) * mm});
            skLineSegment(sketch, "E294.6.3.6", {"start": v(18.73, -317.5) * mm, "end": v(18.73, -342.9) * mm});
            skLineSegment(sketch, "E294.9.3.6", {"start": v(18.73, -342.9) * mm, "end": v(9.2, -342.9) * mm});
            skLineSegment(sketch, "E294.12.3.6", {"start": v(9.2, -352.43) * mm, "end": v(18.73, -352.43) * mm});
            skLineSegment(sketch, "E294.15.3.6", {"start": v(18.73, -352.43) * mm, "end": v(18.73, -358.77) * mm});
            skLineSegment(sketch, "E294.18.3.6", {"start": v(9.2, -358.77) * mm, "end": v(18.73, -358.77) * mm});
            skLineSegment(sketch, "E294.21.3.6", {"start": v(9.2, -352.43) * mm, "end": v(9.2, -358.77) * mm});
            skLineSegment(sketch, "E294.0.3.7", {"start": v(9.2, -368.3) * mm, "end": v(9.2, -393.7) * mm});
            skLineSegment(sketch, "E294.3.3.7", {"start": v(18.73, -368.3) * mm, "end": v(9.2, -368.3) * mm});
            skLineSegment(sketch, "E294.6.3.7", {"start": v(18.73, -368.3) * mm, "end": v(18.73, -393.7) * mm});
            skLineSegment(sketch, "E294.9.3.7", {"start": v(18.73, -393.7) * mm, "end": v(9.2, -393.7) * mm});
            skLineSegment(sketch, "E294.12.3.7", {"start": v(9.2, -403.23) * mm, "end": v(18.73, -403.23) * mm});
            skLineSegment(sketch, "E294.15.3.7", {"start": v(18.73, -403.23) * mm, "end": v(18.73, -409.57) * mm});
            skLineSegment(sketch, "E294.18.3.7", {"start": v(9.2, -409.57) * mm, "end": v(18.73, -409.57) * mm});
            skLineSegment(sketch, "E294.21.3.7", {"start": v(9.2, -403.23) * mm, "end": v(9.2, -409.57) * mm});
            skLineSegment(sketch, "E294.0.3.8", {"start": v(9.2, -419.1) * mm, "end": v(9.2, -444.5) * mm});
            skLineSegment(sketch, "E294.3.3.8", {"start": v(18.73, -419.1) * mm, "end": v(9.2, -419.1) * mm});
            skLineSegment(sketch, "E294.6.3.8", {"start": v(18.73, -419.1) * mm, "end": v(18.73, -444.5) * mm});
            skLineSegment(sketch, "E294.9.3.8", {"start": v(18.73, -444.5) * mm, "end": v(9.2, -444.5) * mm});
            skLineSegment(sketch, "E294.12.3.8", {"start": v(9.2, -454.03) * mm, "end": v(18.73, -454.03) * mm});
            skLineSegment(sketch, "E294.15.3.8", {"start": v(18.73, -454.03) * mm, "end": v(18.73, -460.38) * mm});
            skLineSegment(sketch, "E294.18.3.8", {"start": v(9.2, -460.38) * mm, "end": v(18.73, -460.38) * mm});
            skLineSegment(sketch, "E294.21.3.8", {"start": v(9.2, -454.03) * mm, "end": v(9.2, -460.38) * mm});
            skLineSegment(sketch, "E294.0.3.9", {"start": v(9.2, -469.9) * mm, "end": v(9.2, -495.3) * mm});
            skLineSegment(sketch, "E294.3.3.9", {"start": v(18.73, -469.9) * mm, "end": v(9.2, -469.9) * mm});
            skLineSegment(sketch, "E294.6.3.9", {"start": v(18.73, -469.9) * mm, "end": v(18.73, -495.3) * mm});
            skLineSegment(sketch, "E294.9.3.9", {"start": v(18.73, -495.3) * mm, "end": v(9.2, -495.3) * mm});
            skLineSegment(sketch, "E294.12.3.9", {"start": v(9.2, -504.82) * mm, "end": v(18.73, -504.82) * mm});
            skLineSegment(sketch, "E294.15.3.9", {"start": v(18.73, -504.82) * mm, "end": v(18.73, -511.18) * mm});
            skLineSegment(sketch, "E294.18.3.9", {"start": v(9.2, -511.18) * mm, "end": v(18.73, -511.18) * mm});
            skLineSegment(sketch, "E294.21.3.9", {"start": v(9.2, -504.82) * mm, "end": v(9.2, -511.18) * mm});
            skLineSegment(sketch, "E294.0.3.10", {"start": v(9.2, -520.7) * mm, "end": v(9.2, -546.1) * mm});
            skLineSegment(sketch, "E294.3.3.10", {"start": v(18.73, -520.7) * mm, "end": v(9.2, -520.7) * mm});
            skLineSegment(sketch, "E294.6.3.10", {"start": v(18.73, -520.7) * mm, "end": v(18.73, -546.1) * mm});
            skLineSegment(sketch, "E294.9.3.10", {"start": v(18.73, -546.1) * mm, "end": v(9.2, -546.1) * mm});
            skLineSegment(sketch, "E294.12.3.10", {"start": v(9.2, -555.62) * mm, "end": v(18.73, -555.62) * mm});
            skLineSegment(sketch, "E294.15.3.10", {"start": v(18.73, -555.62) * mm, "end": v(18.73, -561.98) * mm});
            skLineSegment(sketch, "E294.18.3.10", {"start": v(9.2, -561.98) * mm, "end": v(18.73, -561.98) * mm});
            skLineSegment(sketch, "E294.21.3.10", {"start": v(9.2, -555.62) * mm, "end": v(9.2, -561.98) * mm});
            skLineSegment(sketch, "E294.0.3.11", {"start": v(9.2, -571.5) * mm, "end": v(9.2, -596.9) * mm});
            skLineSegment(sketch, "E294.3.3.11", {"start": v(18.73, -571.5) * mm, "end": v(9.2, -571.5) * mm});
            skLineSegment(sketch, "E294.6.3.11", {"start": v(18.73, -571.5) * mm, "end": v(18.73, -596.9) * mm});
            skLineSegment(sketch, "E294.9.3.11", {"start": v(18.73, -596.9) * mm, "end": v(9.2, -596.9) * mm});
            skLineSegment(sketch, "E295.MirrorCS", {"start": v(152.08, -307.98) * mm, "end": v(142.56, -307.98) * mm});
            skLineSegment(sketch, "E296.MirrorCS", {"start": v(142.56, -301.63) * mm, "end": v(142.56, -307.98) * mm});
            skLineSegment(sketch, "E297.MirrorCS", {"start": v(152.08, -301.63) * mm, "end": v(152.08, -307.98) * mm});
            skLineSegment(sketch, "E298.MirrorCS", {"start": v(152.08, -301.63) * mm, "end": v(142.56, -301.63) * mm});
            skLineSegment(sketch, "E299.MirrorCS", {"start": v(152.08, -352.43) * mm, "end": v(142.56, -352.43) * mm});
            skLineSegment(sketch, "E300.MirrorCS", {"start": v(152.08, -352.43) * mm, "end": v(152.08, -358.77) * mm});
            skLineSegment(sketch, "E301.MirrorCS", {"start": v(142.56, -352.43) * mm, "end": v(142.56, -358.77) * mm});
            skLineSegment(sketch, "E302.MirrorCS", {"start": v(152.08, -358.77) * mm, "end": v(142.56, -358.77) * mm});
            skLineSegment(sketch, "E303.MirrorCS", {"start": v(152.08, -409.57) * mm, "end": v(142.56, -409.57) * mm});
            skLineSegment(sketch, "E304.MirrorCS", {"start": v(142.56, -403.23) * mm, "end": v(142.56, -409.57) * mm});
            skLineSegment(sketch, "E305.MirrorCS", {"start": v(152.08, -403.23) * mm, "end": v(152.08, -409.57) * mm});
            skLineSegment(sketch, "E306.MirrorCS", {"start": v(152.08, -403.23) * mm, "end": v(142.56, -403.23) * mm});
            skLineSegment(sketch, "E307.MirrorCS", {"start": v(142.56, -454.03) * mm, "end": v(142.56, -460.38) * mm});
            skLineSegment(sketch, "E308.MirrorCS", {"start": v(152.08, -454.03) * mm, "end": v(142.56, -454.03) * mm});
            skLineSegment(sketch, "E309.MirrorCS", {"start": v(152.08, -454.03) * mm, "end": v(152.08, -460.38) * mm});
            skLineSegment(sketch, "E310.MirrorCS", {"start": v(152.08, -460.38) * mm, "end": v(142.56, -460.38) * mm});
            skLineSegment(sketch, "E311.MirrorCS", {"start": v(152.08, -504.82) * mm, "end": v(152.08, -511.18) * mm});
            skLineSegment(sketch, "E312.MirrorCS", {"start": v(152.08, -511.18) * mm, "end": v(142.56, -511.18) * mm});
            skLineSegment(sketch, "E313.MirrorCS", {"start": v(142.56, -504.82) * mm, "end": v(142.56, -511.18) * mm});
            skLineSegment(sketch, "E314.MirrorCS", {"start": v(152.08, -504.82) * mm, "end": v(142.56, -504.82) * mm});
            skLineSegment(sketch, "E315.MirrorCS", {"start": v(152.08, -555.62) * mm, "end": v(142.56, -555.62) * mm});
            skLineSegment(sketch, "E316.MirrorCS", {"start": v(152.08, -555.62) * mm, "end": v(152.08, -561.98) * mm});
            skLineSegment(sketch, "E317.MirrorCS", {"start": v(142.56, -555.62) * mm, "end": v(142.56, -561.98) * mm});
            skLineSegment(sketch, "E318.MirrorCS", {"start": v(152.08, -561.98) * mm, "end": v(142.56, -561.98) * mm});
            skLineSegment(sketch, "E319.MirrorCS", {"start": v(152.08, -250.83) * mm, "end": v(142.56, -250.83) * mm});
            skLineSegment(sketch, "E320.MirrorCS", {"start": v(152.08, -250.83) * mm, "end": v(152.08, -257.18) * mm});
            skLineSegment(sketch, "E321.MirrorCS", {"start": v(142.56, -250.83) * mm, "end": v(142.56, -257.18) * mm});
            skLineSegment(sketch, "E322.MirrorCS", {"start": v(152.08, -257.18) * mm, "end": v(142.56, -257.18) * mm});
            skLineSegment(sketch, "E323.MirrorCS", {"start": v(152.08, -200.02) * mm, "end": v(152.08, -206.37) * mm});
            skLineSegment(sketch, "E324.MirrorCS", {"start": v(142.56, -200.02) * mm, "end": v(142.56, -206.37) * mm});
            skLineSegment(sketch, "E325.MirrorCS", {"start": v(152.08, -200.02) * mm, "end": v(142.56, -200.02) * mm});
            skLineSegment(sketch, "E326.MirrorCS", {"start": v(152.08, -206.37) * mm, "end": v(142.56, -206.37) * mm});
            skLineSegment(sketch, "E327.MirrorCS", {"start": v(152.08, -149.22) * mm, "end": v(142.56, -149.22) * mm});
            skLineSegment(sketch, "E328.MirrorCS", {"start": v(142.56, -149.22) * mm, "end": v(142.56, -155.58) * mm});
            skLineSegment(sketch, "E329.MirrorCS", {"start": v(152.08, -149.22) * mm, "end": v(152.08, -155.58) * mm});
            skLineSegment(sketch, "E330.MirrorCS", {"start": v(152.08, -155.58) * mm, "end": v(142.56, -155.58) * mm});
            skLineSegment(sketch, "E331.MirrorCS", {"start": v(142.56, -98.43) * mm, "end": v(142.56, -104.78) * mm});
            skLineSegment(sketch, "E332.MirrorCS", {"start": v(152.08, -98.43) * mm, "end": v(152.08, -104.78) * mm});
            skLineSegment(sketch, "E333.MirrorCS", {"start": v(152.08, -104.78) * mm, "end": v(142.56, -104.78) * mm});
            skLineSegment(sketch, "E334.MirrorCS", {"start": v(152.08, -98.43) * mm, "end": v(142.56, -98.43) * mm});
            skLineSegment(sketch, "E335.MirrorCS", {"start": v(152.08, -47.63) * mm, "end": v(142.56, -47.63) * mm});
            skLineSegment(sketch, "E336.MirrorCS", {"start": v(142.56, -47.63) * mm, "end": v(142.56, -53.98) * mm});
            skLineSegment(sketch, "E337.MirrorCS", {"start": v(152.08, -53.98) * mm, "end": v(142.56, -53.98) * mm});
            skLineSegment(sketch, "E338.MirrorCS", {"start": v(152.08, -47.63) * mm, "end": v(152.08, -53.98) * mm});
            skLineSegment(sketch, "E339.MirrorCS", {"start": v(142.56, -292.1) * mm, "end": v(152.08, -292.1) * mm});
            skLineSegment(sketch, "E340.MirrorCS", {"start": v(142.56, -266.7) * mm, "end": v(152.08, -266.7) * mm});
            skLineSegment(sketch, "E341.MirrorCS", {"start": v(142.56, -266.7) * mm, "end": v(142.56, -292.1) * mm});
            skLineSegment(sketch, "E342.MirrorCS", {"start": v(152.08, -266.7) * mm, "end": v(152.08, -292.1) * mm});
            skLineSegment(sketch, "E343.MirrorCS", {"start": v(142.56, -317.5) * mm, "end": v(142.56, -342.9) * mm});
            skLineSegment(sketch, "E344.MirrorCS", {"start": v(142.56, -342.9) * mm, "end": v(152.08, -342.9) * mm});
            skLineSegment(sketch, "E345.MirrorCS", {"start": v(142.56, -317.5) * mm, "end": v(152.08, -317.5) * mm});
            skLineSegment(sketch, "E346.MirrorCS", {"start": v(152.08, -317.5) * mm, "end": v(152.08, -342.9) * mm});
            skLineSegment(sketch, "E347.MirrorCS", {"start": v(142.56, -393.7) * mm, "end": v(152.08, -393.7) * mm});
            skLineSegment(sketch, "E348.MirrorCS", {"start": v(142.56, -368.3) * mm, "end": v(142.56, -393.7) * mm});
            skLineSegment(sketch, "E349.MirrorCS", {"start": v(142.56, -368.3) * mm, "end": v(152.08, -368.3) * mm});
            skLineSegment(sketch, "E350.MirrorCS", {"start": v(152.08, -368.3) * mm, "end": v(152.08, -393.7) * mm});
            skLineSegment(sketch, "E351.MirrorCS", {"start": v(142.56, -419.1) * mm, "end": v(142.56, -444.5) * mm});
            skLineSegment(sketch, "E352.MirrorCS", {"start": v(142.56, -444.5) * mm, "end": v(152.08, -444.5) * mm});
            skLineSegment(sketch, "E353.MirrorCS", {"start": v(142.56, -419.1) * mm, "end": v(152.08, -419.1) * mm});
            skLineSegment(sketch, "E354.MirrorCS", {"start": v(152.08, -419.1) * mm, "end": v(152.08, -444.5) * mm});
            skLineSegment(sketch, "E355.MirrorCS", {"start": v(142.56, -495.3) * mm, "end": v(152.08, -495.3) * mm});
            skLineSegment(sketch, "E356.MirrorCS", {"start": v(142.56, -469.9) * mm, "end": v(142.56, -495.3) * mm});
            skLineSegment(sketch, "E357.MirrorCS", {"start": v(142.56, -469.9) * mm, "end": v(152.08, -469.9) * mm});
            skLineSegment(sketch, "E358.MirrorCS", {"start": v(152.08, -469.9) * mm, "end": v(152.08, -495.3) * mm});
            skLineSegment(sketch, "E359.MirrorCS", {"start": v(142.56, -520.7) * mm, "end": v(142.56, -546.1) * mm});
            skLineSegment(sketch, "E360.MirrorCS", {"start": v(142.56, -546.1) * mm, "end": v(152.08, -546.1) * mm});
            skLineSegment(sketch, "E361.MirrorCS", {"start": v(142.56, -520.7) * mm, "end": v(152.08, -520.7) * mm});
            skLineSegment(sketch, "E362.MirrorCS", {"start": v(152.08, -520.7) * mm, "end": v(152.08, -546.1) * mm});
            skLineSegment(sketch, "E363.MirrorCS", {"start": v(142.56, -596.9) * mm, "end": v(152.08, -596.9) * mm});
            skLineSegment(sketch, "E364.MirrorCS", {"start": v(142.56, -571.5) * mm, "end": v(152.08, -571.5) * mm});
            skLineSegment(sketch, "E365.MirrorCS", {"start": v(142.56, -571.5) * mm, "end": v(142.56, -596.9) * mm});
            skLineSegment(sketch, "E366.MirrorCS", {"start": v(152.08, -571.5) * mm, "end": v(152.08, -596.9) * mm});
            skLineSegment(sketch, "E367.MirrorCS", {"start": v(142.56, -241.3) * mm, "end": v(152.08, -241.3) * mm});
            skLineSegment(sketch, "E368.MirrorCS", {"start": v(142.56, -215.9) * mm, "end": v(152.08, -215.9) * mm});
            skLineSegment(sketch, "E369.MirrorCS", {"start": v(142.56, -215.9) * mm, "end": v(142.56, -241.3) * mm});
            skLineSegment(sketch, "E370.MirrorCS", {"start": v(152.08, -215.9) * mm, "end": v(152.08, -241.3) * mm});
            skLineSegment(sketch, "E371.MirrorCS", {"start": v(142.56, -190.5) * mm, "end": v(152.08, -190.5) * mm});
            skLineSegment(sketch, "E372.MirrorCS", {"start": v(142.56, -165.1) * mm, "end": v(152.08, -165.1) * mm});
            skLineSegment(sketch, "E373.MirrorCS", {"start": v(142.56, -165.1) * mm, "end": v(142.56, -190.5) * mm});
            skLineSegment(sketch, "E374.MirrorCS", {"start": v(152.08, -165.1) * mm, "end": v(152.08, -190.5) * mm});
            skLineSegment(sketch, "E375.MirrorCS", {"start": v(142.56, -114.3) * mm, "end": v(142.56, -139.7) * mm});
            skLineSegment(sketch, "E376.MirrorCS", {"start": v(142.56, -139.7) * mm, "end": v(152.08, -139.7) * mm});
            skLineSegment(sketch, "E377.MirrorCS", {"start": v(142.56, -114.3) * mm, "end": v(152.08, -114.3) * mm});
            skLineSegment(sketch, "E378.MirrorCS", {"start": v(152.08, -114.3) * mm, "end": v(152.08, -139.7) * mm});
            skLineSegment(sketch, "E379.MirrorCS", {"start": v(142.56, -88.9) * mm, "end": v(152.08, -88.9) * mm});
            skLineSegment(sketch, "E380.MirrorCS", {"start": v(142.56, -63.5) * mm, "end": v(152.08, -63.5) * mm});
            skLineSegment(sketch, "E381.MirrorCS", {"start": v(142.56, -63.5) * mm, "end": v(142.56, -88.9) * mm});
            skLineSegment(sketch, "E382.MirrorCS", {"start": v(152.08, -63.5) * mm, "end": v(152.08, -88.9) * mm});
            skLineSegment(sketch, "E383.MirrorCS", {"start": v(142.56, -38.1) * mm, "end": v(152.08, -38.1) * mm});
            skLineSegment(sketch, "E384.MirrorCS", {"start": v(142.56, -12.7) * mm, "end": v(152.08, -12.7) * mm});
            skLineSegment(sketch, "E385.MirrorCS", {"start": v(152.08, -12.7) * mm, "end": v(152.08, -38.1) * mm});
            skLineSegment(sketch, "E386.MirrorCS", {"start": v(142.56, -12.7) * mm, "end": v(142.56, -38.1) * mm});
            skSolve(sketch);
        }
        {
            var Q0;
            Q0 = qSketchRegion(id + "F2", true);
            extrude(context, id + "F3", {"entities" : qUnion([Q0]), "operationType" : NewBodyOperationType.REMOVE, "endBound" : BoundingType.THROUGH_ALL, "oppositeDirection" : true, "depth" : 25.4 * mm, "offsetDistance" : 25.4 * mm});
        }
    });
